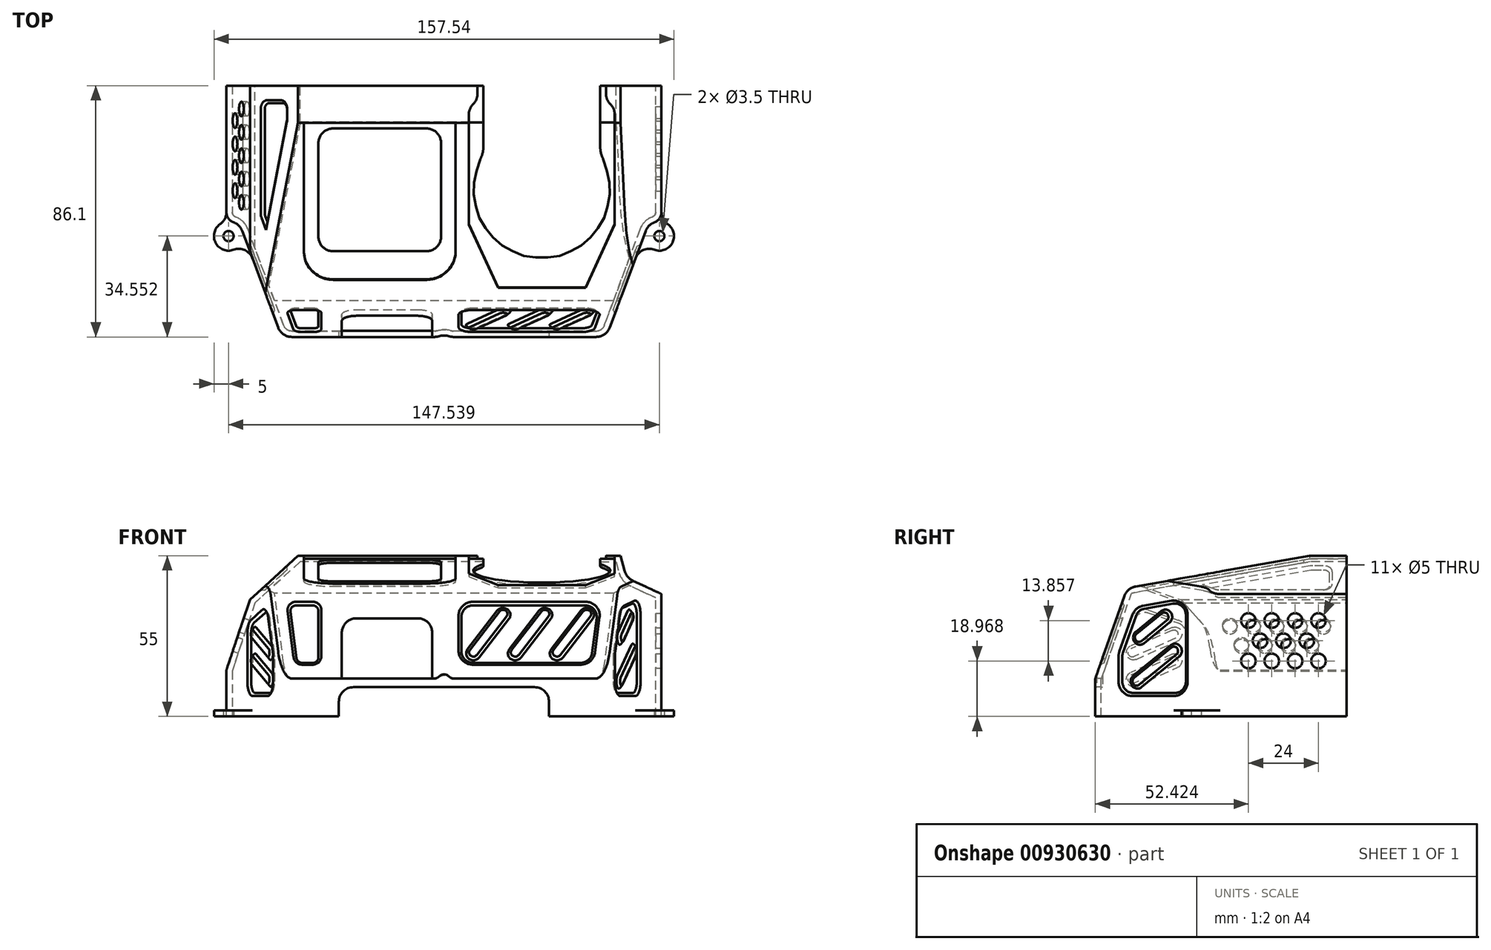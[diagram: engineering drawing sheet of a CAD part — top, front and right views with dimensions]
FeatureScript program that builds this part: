
annotation { "Feature Type Name" : "Feature", "Feature Type Description" : "" }
export const myFeature = defineFeature(function(context is Context, id is Id, definition is map)
    precondition{}
    {
        {
            var Q0;
            Q0=qCreatedBy(makeId("Top.planeOp"),FACE);
            var sketch = newSketch(context, id + "F0", { "sketchPlane" : qUnion([Q0])});
            skLineSegment(sketch, "E0.bottom", {"start": v(-53.5, -83.4) * mm, "end": v(-5, -83.4) * mm, "construction": true});
            skLineSegment(sketch, "E0.top", {"start": v(-51.5, 90.4) * mm, "end": v(51.5, 90.4) * mm, "construction": true});
            skLineSegment(sketch, "E0.left", {"start": v(-71.5, -35) * mm, "end": v(-71.5, 0) * mm, "construction": true});
            skLineSegment(sketch, "E0.right", {"start": v(71.5, -35) * mm, "end": v(71.5, 0) * mm, "construction": true});
            skLineSegment(sketch, "E1", {"start": v(-71.5, -35) * mm, "end": v(-68.01, -44.37) * mm, "construction": true});
            skLineSegment(sketch, "E2", {"start": v(53.5, -83.4) * mm, "end": v(64.53, -53.75) * mm, "construction": true});
            skPoint(sketch, "E3.orphan", {"position": v(-71.5, -83.4) * mm});
            skPoint(sketch, "E4.orphan", {"position": v(71.5, -83.4) * mm});
            skLineSegment(sketch, "E5", {"start": v(-71.5, 0) * mm, "end": v(-69.34, 9.76) * mm, "construction": true});
            skLineSegment(sketch, "E6", {"start": v(51.5, 90.4) * mm, "end": v(55.82, 70.87) * mm, "construction": true});
            skPoint(sketch, "E7.orphan", {"position": v(-71.5, 90.4) * mm});
            skPoint(sketch, "E8.orphan", {"position": v(71.5, 90.4) * mm});
            skLineSegment(sketch, "E9", {"start": v(-5, -83.4) * mm, "end": v(-5, -91.4) * mm, "construction": true});
            skLineSegment(sketch, "E10", {"start": v(5, -91.4) * mm, "end": v(5, -83.4) * mm, "construction": true});
            skArc(sketch, "E11", {"start": v(-5, -91.4) * mm, "mid": v(0, -96.4) * mm, "end": v(5, -91.4) * mm, "construction": true});
            skLineSegment(sketch, "E12.trimOffspring", {"start": v(5, -83.4) * mm, "end": v(53.5, -83.4) * mm, "construction": true});
            skLineSegment(sketch, "E13", {"start": v(-68.01, -44.37) * mm, "end": v(-75.51, -47.16) * mm, "construction": true});
            skLineSegment(sketch, "E14", {"start": v(-72.03, -56.53) * mm, "end": v(-64.53, -53.75) * mm, "construction": true});
            skArc(sketch, "E15", {"start": v(-75.51, -47.16) * mm, "mid": v(-78.46, -53.6) * mm, "end": v(-72.03, -56.53) * mm, "construction": true});
            skLineSegment(sketch, "E16.trimOffspring", {"start": v(-64.53, -53.75) * mm, "end": v(-53.5, -83.4) * mm, "construction": true});
            skLineSegment(sketch, "E17", {"start": v(68.01, -44.37) * mm, "end": v(75.51, -47.16) * mm, "construction": true});
            skLineSegment(sketch, "E18", {"start": v(72.03, -56.53) * mm, "end": v(64.53, -53.75) * mm, "construction": true});
            skArc(sketch, "E19", {"start": v(72.03, -56.53) * mm, "mid": v(78.46, -53.6) * mm, "end": v(75.51, -47.16) * mm, "construction": true});
            skLineSegment(sketch, "E20.trimOffspring", {"start": v(68.01, -44.37) * mm, "end": v(71.5, -35) * mm, "construction": true});
            skLineSegment(sketch, "E21", {"start": v(-69.34, 9.76) * mm, "end": v(-77.15, 11.5) * mm, "construction": true});
            skLineSegment(sketch, "E22.trimOffspring", {"start": v(-65.02, 29.3) * mm, "end": v(-57.98, 61.1) * mm, "construction": true});
            skLineSegment(sketch, "E23", {"start": v(69.34, 9.76) * mm, "end": v(77.15, 11.5) * mm, "construction": true});
            skLineSegment(sketch, "E24.trimOffspring", {"start": v(69.34, 9.76) * mm, "end": v(71.5, 0) * mm, "construction": true});
            skLineSegment(sketch, "E25", {"start": v(-57.98, 61.1) * mm, "end": v(-65.8, 62.84) * mm, "construction": true});
            skLineSegment(sketch, "E26", {"start": v(-55.82, 70.87) * mm, "end": v(-63.63, 72.6) * mm, "construction": true});
            skArc(sketch, "E27", {"start": v(-63.63, 72.6) * mm, "mid": v(-69.6, 68.8) * mm, "end": v(-65.8, 62.84) * mm, "construction": true});
            skLineSegment(sketch, "E28.trimOffspring", {"start": v(-55.82, 70.87) * mm, "end": v(-51.5, 90.4) * mm, "construction": true});
            skLineSegment(sketch, "E29", {"start": v(57.98, 61.1) * mm, "end": v(65.8, 62.84) * mm, "construction": true});
            skLineSegment(sketch, "E30", {"start": v(55.82, 70.87) * mm, "end": v(63.63, 72.6) * mm, "construction": true});
            skArc(sketch, "E31", {"start": v(65.8, 62.84) * mm, "mid": v(69.6, 68.8) * mm, "end": v(63.63, 72.6) * mm, "construction": true});
            skLineSegment(sketch, "E32.trimOffspring", {"start": v(57.98, 61.1) * mm, "end": v(65.02, 29.3) * mm, "construction": true});
            skCircle(sketch, "E33", {"center": v(-73.77, -51.85) * mm, "radius": 1.75 * mm, "construction": true});
            skCircle(sketch, "E34", {"center": v(-76.07, 16.37) * mm, "radius": 1.75 * mm, "construction": true});
            skCircle(sketch, "E35", {"center": v(-64.71, 67.72) * mm, "radius": 1.75 * mm, "construction": true});
            skCircle(sketch, "E36", {"center": v(64.71, 67.72) * mm, "radius": 1.75 * mm, "construction": true});
            skCircle(sketch, "E37", {"center": v(76.07, 16.37) * mm, "radius": 1.75 * mm, "construction": true});
            skCircle(sketch, "E38", {"center": v(73.77, -51.85) * mm, "radius": 1.75 * mm, "construction": true});
            skCircle(sketch, "E39", {"center": v(0, -91.4) * mm, "radius": 1.75 * mm, "construction": true});
            skCircle(sketch, "E40", {"center": v(66.5, -30) * mm, "radius": 1.75 * mm, "construction": true});
            skCircle(sketch, "E41", {"center": v(28.5, 0.5) * mm, "radius": 1.75 * mm, "construction": true});
            skCircle(sketch, "E42", {"center": v(-57, -10) * mm, "radius": 1.75 * mm, "construction": true});
            skCircle(sketch, "E43", {"center": v(-57, -56) * mm, "radius": 1.75 * mm, "construction": true});
            skCircle(sketch, "E44", {"center": v(28.5, -66.5) * mm, "radius": 1.75 * mm, "construction": true});
            skArc(sketch, "E45", {"start": v(-59.92, -5.94) * mm, "mid": v(-61.45, -7.72) * mm, "end": v(-62, -10) * mm, "construction": true});
            skLineSegment(sketch, "E46", {"start": v(-62, -10) * mm, "end": v(-62, -56) * mm, "construction": true});
            skArc(sketch, "E47", {"start": v(-62, -56) * mm, "mid": v(-61.43, -58.31) * mm, "end": v(-59.86, -60.1) * mm, "construction": true});
            skArc(sketch, "E48", {"start": v(28.5, -71.5) * mm, "mid": v(32.04, -70.04) * mm, "end": v(33.5, -66.5) * mm, "construction": true});
            skArc(sketch, "E49", {"start": v(33.5, 0.5) * mm, "mid": v(32.04, 4.04) * mm, "end": v(28.5, 5.5) * mm, "construction": true});
            skArc(sketch, "E50", {"start": v(71.5, -9.75) * mm, "mid": v(69.95, -6.38) * mm, "end": v(66.5, -5) * mm, "construction": true});
            skArc(sketch, "E51", {"start": v(58.36, -61) * mm, "mid": v(61.2, -60.1) * mm, "end": v(63.04, -57.74) * mm, "construction": true});
            skLineSegment(sketch, "E52", {"start": v(28.5, -71.5) * mm, "end": v(-43.5, -71.5) * mm, "construction": true});
            skLineSegment(sketch, "E53", {"start": v(-43.5, -71.5) * mm, "end": v(-59.86, -60.1) * mm, "construction": true});
            skLineSegment(sketch, "E54", {"start": v(-59.92, -5.94) * mm, "end": v(-44, 5.5) * mm, "construction": true});
            skLineSegment(sketch, "E55", {"start": v(-44, 5.5) * mm, "end": v(28.5, 5.5) * mm, "construction": true});
            skLineSegment(sketch, "E56", {"start": v(33.5, 0.5) * mm, "end": v(33.5, -5) * mm, "construction": true});
            skLineSegment(sketch, "E57", {"start": v(33.5, -5) * mm, "end": v(66.5, -5) * mm, "construction": true});
            skLineSegment(sketch, "E58", {"start": v(33.5, -66.5) * mm, "end": v(33.5, -61) * mm, "construction": true});
            skLineSegment(sketch, "E59", {"start": v(33.5, -61) * mm, "end": v(58.36, -61) * mm, "construction": true});
            skCircle(sketch, "E60", {"center": v(-22, -36) * mm, "radius": 18.8 * mm, "construction": true});
            skCircle(sketch, "E61", {"center": v(20.5, -18) * mm, "radius": 1.5 * mm, "construction": true});
            skCircle(sketch, "E62", {"center": v(46.5, -18) * mm, "radius": 1.5 * mm, "construction": true});
            skCircle(sketch, "E63", {"center": v(20.5, -48) * mm, "radius": 1.5 * mm, "construction": true});
            skCircle(sketch, "E64", {"center": v(46.5, -48) * mm, "radius": 1.5 * mm, "construction": true});
            skLineSegment(sketch, "E65", {"start": v(17, -6) * mm, "end": v(17, -48) * mm, "construction": true});
            skLineSegment(sketch, "E66", {"start": v(50, -6) * mm, "end": v(50, -48) * mm, "construction": true});
            skLineSegment(sketch, "E67", {"start": v(20.5, -51.5) * mm, "end": v(46.5, -51.5) * mm, "construction": true});
            skArc(sketch, "E68", {"start": v(17, -48) * mm, "mid": v(18.03, -50.47) * mm, "end": v(20.5, -51.5) * mm, "construction": true});
            skArc(sketch, "E69", {"start": v(46.5, -51.5) * mm, "mid": v(48.97, -50.47) * mm, "end": v(50, -48) * mm, "construction": true});
            skLineSegment(sketch, "E70", {"start": v(17, -6) * mm, "end": v(50, -6) * mm, "construction": true});
            skLineSegment(sketch, "E71", {"start": v(-80.95, 17.45) * mm, "end": v(-78.8, 27.22) * mm, "construction": true});
            skArc(sketch, "E72", {"start": v(-80.95, 17.45) * mm, "mid": v(-80.29, 13.69) * mm, "end": v(-77.15, 11.5) * mm, "construction": true});
            skArc(sketch, "E73", {"start": v(-72.83, 31.02) * mm, "mid": v(-76.6, 30.35) * mm, "end": v(-78.8, 27.22) * mm, "construction": true});
            skLineSegment(sketch, "E74", {"start": v(-72.83, 31.02) * mm, "end": v(-65.02, 29.3) * mm, "construction": true});
            skCircle(sketch, "E75", {"center": v(-73.91, 26.14) * mm, "radius": 1.75 * mm, "construction": true});
            skLineSegment(sketch, "E76", {"start": v(65.02, 29.3) * mm, "end": v(72.83, 31.02) * mm, "construction": true});
            skArc(sketch, "E77", {"start": v(78.8, 27.22) * mm, "mid": v(76.6, 30.35) * mm, "end": v(72.83, 31.02) * mm, "construction": true});
            skArc(sketch, "E78", {"start": v(77.15, 11.5) * mm, "mid": v(80.29, 13.69) * mm, "end": v(80.95, 17.45) * mm, "construction": true});
            skLineSegment(sketch, "E79", {"start": v(78.8, 27.22) * mm, "end": v(80.95, 17.45) * mm, "construction": true});
            skCircle(sketch, "E80", {"center": v(73.91, 26.14) * mm, "radius": 1.75 * mm, "construction": true});
            skLineSegment(sketch, "E81", {"start": v(-43, -19.9) * mm, "end": v(-43, -52.1) * mm, "construction": true});
            skLineSegment(sketch, "E82", {"start": v(-38.1, -57) * mm, "end": v(-5.9, -57) * mm, "construction": true});
            skLineSegment(sketch, "E83", {"start": v(-1, -52.1) * mm, "end": v(-1, -19.9) * mm, "construction": true});
            skLineSegment(sketch, "E84", {"start": v(-5.9, -15) * mm, "end": v(-38.1, -15) * mm, "construction": true});
            skArc(sketch, "E85", {"start": v(-38.1, -15) * mm, "mid": v(-41.56, -16.44) * mm, "end": v(-43, -19.9) * mm, "construction": true});
            skArc(sketch, "E86", {"start": v(-43, -52.1) * mm, "mid": v(-41.56, -55.56) * mm, "end": v(-38.1, -57) * mm, "construction": true});
            skArc(sketch, "E87", {"start": v(-1, -19.9) * mm, "mid": v(-2.44, -16.44) * mm, "end": v(-5.9, -15) * mm, "construction": true});
            skArc(sketch, "E88", {"start": v(-5.9, -57) * mm, "mid": v(-2.44, -55.56) * mm, "end": v(-1, -52.1) * mm, "construction": true});
            skCircle(sketch, "E89", {"center": v(33.5, -36) * mm, "radius": 23.5 * mm, "construction": true});
            skSolve(sketch);
        }
        {
            var Q0;
            Q0=qCreatedBy(makeId("Top.planeOp"),FACE);
            var sketch = newSketch(context, id + "F1", { "sketchPlane" : qUnion([Q0])});
            skLineSegment(sketch, "E90", {"start": v(-74.5, 0) * mm, "end": v(74.5, 0) * mm});
            skLineSegment(sketch, "E91", {"start": v(-74.5, 0) * mm, "end": v(-74.5, -46.78) * mm});
            skLineSegment(sketch, "E92", {"start": v(74.5, -46.78) * mm, "end": v(74.5, 0) * mm});
            skLineSegment(sketch, "E93", {"start": v(-67.34, -54.8) * mm, "end": v(-55.59, -86.4) * mm});
            skLineSegment(sketch, "E94", {"start": v(55.59, -86.4) * mm, "end": v(67.34, -54.8) * mm});
            skLineSegment(sketch, "E95.trimOffspring", {"start": v(-55.59, -86.4) * mm, "end": v(-2.3, -86.4) * mm});
            skArc(sketch, "E96", {"start": v(-75.51, -47.16) * mm, "mid": v(-78.46, -53.6) * mm, "end": v(-72.03, -56.53) * mm});
            skLineSegment(sketch, "E97", {"start": v(-75.51, -47.16) * mm, "end": v(-74.5, -46.78) * mm});
            skLineSegment(sketch, "E98", {"start": v(-72.03, -56.53) * mm, "end": v(-67.34, -54.8) * mm});
            skLineSegment(sketch, "E99", {"start": v(67.34, -54.8) * mm, "end": v(72.03, -56.53) * mm});
            skLineSegment(sketch, "E100", {"start": v(74.5, -46.78) * mm, "end": v(75.51, -47.16) * mm});
            skArc(sketch, "E101", {"start": v(72.03, -56.53) * mm, "mid": v(78.46, -53.6) * mm, "end": v(75.51, -47.16) * mm});
            skArc(sketch, "E102", {"start": v(2.3, -86.4) * mm, "mid": v(0, -85.9) * mm, "end": v(-2.3, -86.4) * mm});
            skLineSegment(sketch, "E103.trimOffspring", {"start": v(2.3, -86.4) * mm, "end": v(55.59, -86.4) * mm});
            skSolve(sketch);
        }
        {
            var Q0;
            Q0=qSketchRegion(id+"F1",true);
            extrude(context, id + "F2", {"entities" : qUnion([Q0]), "depth" : 55 * mm, "offsetDistance" : 25 * mm});
        }
        {
            var Q0;
            Q0=makeQuery(id+"F2.opExtrude","SWEPT_EDGE",EDGE,{"disambiguationData":[OSD([sQuery(id+"F1.wireOp",EDGE,"E93"),sQuery(id+"F1.wireOp",EDGE,"3QDwpkBZ-OKoi-ct7H-oCOv-kOIZgjfHdJRy")])]});
            var Q1;
            Q1=makeQuery(id+"F2.opExtrude","SWEPT_EDGE",EDGE,{"disambiguationData":[OSD([sQuery(id+"F1.wireOp",EDGE,"E93"),sQuery(id+"F1.wireOp",EDGE,"E95.trimOffspring")])]});
            var Q2;
            Q2=makeQuery(id+"F2.opExtrude","SWEPT_EDGE",EDGE,{"disambiguationData":[OSD([sQuery(id+"F1.wireOp",EDGE,"E94"),sQuery(id+"F1.wireOp",EDGE,"E95.trimOffspring")])]});
            var Q3;
            Q3=makeQuery(id+"F2.opExtrude","SWEPT_EDGE",EDGE,{"disambiguationData":[OSD([sQuery(id+"F1.wireOp",EDGE,"E94"),sQuery(id+"F1.wireOp",EDGE,"8AUUyvxQ-JrK8-Af2P-wNva-NpeGH8QvNI9z")])]});
            var Q4;
            Q4=makeQuery(id+"F2.opExtrude","SWEPT_EDGE",EDGE,{"disambiguationData":[OSD([sQuery(id+"F1.wireOp",EDGE,"E91"),sQuery(id+"F1.wireOp",EDGE,"E97")])]});
            var Q5;
            Q5=makeQuery(id+"F2.opExtrude","SWEPT_EDGE",EDGE,{"disambiguationData":[OSD([sQuery(id+"F1.wireOp",EDGE,"E92"),sQuery(id+"F1.wireOp",EDGE,"E100")])]});
            var Q6;
            Q6=makeQuery(id+"F2.opExtrude","SWEPT_EDGE",EDGE,{"disambiguationData":[OSD([sQuery(id+"F1.wireOp",EDGE,"E102"),sQuery(id+"F1.wireOp",EDGE,"E103.trimOffspring")])]});
            fillet(context, id + "F3", {"entities" : qUnion([Q0, Q1, Q2, Q3, Q4, Q5, Q6]), "radius" : 5 * mm, "tangentPropagation" : true, "allowEdgeOverflow" : false});
        }
        {
            var Q0;
            Q0=makeQuery(id+"F2.opExtrude","SWEPT_FACE",FACE,{"disambiguationData":[OSD([sQuery(id+"F1.wireOp",EDGE,"E90")])]});
            var sketch = newSketch(context, id + "F4", { "sketchPlane" : qUnion([Q0])});
            skLineSegment(sketch, "E104.bottom", {"start": v(-71.5, 13) * mm, "end": v(71.5, 13) * mm, "construction": true});
            skLineSegment(sketch, "E104.top", {"start": v(-71.5, 10) * mm, "end": v(71.5, 10) * mm, "construction": true});
            skLineSegment(sketch, "E104.left", {"start": v(-71.5, 13) * mm, "end": v(-71.5, 10) * mm, "construction": true});
            skLineSegment(sketch, "E104.right", {"start": v(71.5, 13) * mm, "end": v(71.5, 10) * mm, "construction": true});
            skLineSegment(sketch, "E105.bottom", {"start": v(-71.5, 40) * mm, "end": v(62, 40) * mm, "construction": true});
            skLineSegment(sketch, "E105.top", {"start": v(-71.5, 38) * mm, "end": v(62, 38) * mm, "construction": true});
            skLineSegment(sketch, "E105.left", {"start": v(-71.5, 40) * mm, "end": v(-71.5, 38) * mm, "construction": true});
            skLineSegment(sketch, "E105.right", {"start": v(62, 40) * mm, "end": v(62, 38) * mm, "construction": true});
            skLineSegment(sketch, "E106", {"start": v(-71.5, 38) * mm, "end": v(-71.5, 13) * mm, "construction": true});
            skLineSegment(sketch, "E107", {"start": v(-61.5, 38) * mm, "end": v(-61.5, 13) * mm, "construction": true});
            skLineSegment(sketch, "E108", {"start": v(62, 38) * mm, "end": v(62, 13) * mm, "construction": true});
            skLineSegment(sketch, "E109", {"start": v(52, 38) * mm, "end": v(52, 13) * mm, "construction": true});
            skLineSegment(sketch, "E110", {"start": v(-50, 40) * mm, "end": v(-50, 50) * mm, "construction": true});
            skLineSegment(sketch, "E111", {"start": v(-50, 50) * mm, "end": v(-17, 50) * mm, "construction": true});
            skLineSegment(sketch, "E112", {"start": v(-17, 50) * mm, "end": v(-17, 40) * mm, "construction": true});
            skLineSegment(sketch, "E113", {"start": v(43, 40) * mm, "end": v(43, 48) * mm, "construction": true});
            skLineSegment(sketch, "E114", {"start": v(43, 48) * mm, "end": v(1, 48) * mm, "construction": true});
            skLineSegment(sketch, "E115", {"start": v(1, 48) * mm, "end": v(1, 40) * mm, "construction": true});
            skSolve(sketch);
        }
        {
            var Q0;
            Q0=qCreatedBy(makeId("Right.planeOp"),FACE);
            var sketch = newSketch(context, id + "F5", { "sketchPlane" : qUnion([Q0])});
            skLineSegment(sketch, "E116.bottom", {"start": v(5.5, 13) * mm, "end": v(-77.9, 13) * mm, "construction": true});
            skLineSegment(sketch, "E116.top", {"start": v(5.5, 10) * mm, "end": v(-77.9, 10) * mm, "construction": true});
            skLineSegment(sketch, "E116.left", {"start": v(5.5, 13) * mm, "end": v(5.5, 10) * mm, "construction": true});
            skLineSegment(sketch, "E116.right", {"start": v(-77.9, 13) * mm, "end": v(-77.9, 10) * mm, "construction": true});
            skLineSegment(sketch, "E117.bottom", {"start": v(5.5, 40) * mm, "end": v(-71.5, 40) * mm, "construction": true});
            skLineSegment(sketch, "E117.top", {"start": v(5.5, 38) * mm, "end": v(-71.5, 38) * mm, "construction": true});
            skLineSegment(sketch, "E117.left", {"start": v(5.5, 40) * mm, "end": v(5.5, 38) * mm, "construction": true});
            skLineSegment(sketch, "E117.right", {"start": v(-71.5, 40) * mm, "end": v(-71.5, 38) * mm, "construction": true});
            skLineSegment(sketch, "E118", {"start": v(-71.5, 38) * mm, "end": v(-71.5, 13) * mm, "construction": true});
            skLineSegment(sketch, "E119", {"start": v(-61.5, 38) * mm, "end": v(-61.5, 13) * mm, "construction": true});
            skLineSegment(sketch, "E120", {"start": v(5.5, 38) * mm, "end": v(5.5, 13) * mm, "construction": true});
            skLineSegment(sketch, "E121", {"start": v(-4.5, 38) * mm, "end": v(-4.5, 13) * mm, "construction": true});
            skLineSegment(sketch, "E122", {"start": v(-15, 40) * mm, "end": v(-15, 48) * mm, "construction": true});
            skLineSegment(sketch, "E123", {"start": v(-15, 48) * mm, "end": v(-57, 48) * mm, "construction": true});
            skLineSegment(sketch, "E124", {"start": v(-57, 48) * mm, "end": v(-57, 40) * mm, "construction": true});
            skSolve(sketch);
        }
        {
            var Q0;
            Q0=makeQuery(id+"F2.opExtrude","SWEPT_FACE",FACE,{"disambiguationData":[OSD([sQuery(id+"F1.wireOp",EDGE,"E91")])]});
            var sketch = newSketch(context, id + "F6", { "sketchPlane" : qUnion([Q0])});
            skLineSegment(sketch, "E125", {"start": v(13, 55) * mm, "end": v(75.5, 44) * mm});
            skLineSegment(sketch, "E126", {"start": v(75.5, 44) * mm, "end": v(86.4, 13) * mm});
            skLineSegment(sketch, "E127", {"start": v(13, 55) * mm, "end": v(86.4, 55) * mm});
            skLineSegment(sketch, "E128", {"start": v(86.4, 55) * mm, "end": v(86.4, 13) * mm});
            skSolve(sketch);
        }
        {
            var Q0;
            Q0=qSketchRegion(id+"F6",true);
            extrude(context, id + "F7", {"entities" : qUnion([Q0]), "operationType" : NewBodyOperationType.REMOVE, "endBound" : BoundingType.THROUGH_ALL, "oppositeDirection" : true, "depth" : 25 * mm, "offsetDistance" : 25 * mm});
        }
        {
            var Q0;
            Q0=qSketchRegion(id+"F6",true);
            extrude(context, id + "F8", {"entities" : qUnion([Q0]), "operationType" : NewBodyOperationType.REMOVE, "endBound" : BoundingType.THROUGH_ALL, "depth" : 25 * mm, "offsetDistance" : 25 * mm});
        }
        {
            var Q0;
            {var subQ0=sQuery(id+"F1.wireOp",EDGE,"E90");Q0=makeQuery(id+"F4.imprint","IMPRINT",FACE,{"disambiguationData":[TD([[makeQuery(id+"F4.imprint","IMPRINT",EDGE,{"derivedFrom":makeQuery(id+"F2.opExtrude","CAP_EDGE",EDGE,{"disambiguationData":[OSD([subQ0])],"isStart":true})}),-1.0]])]});}
            var sketch = newSketch(context, id + "F9", { "sketchPlane" : qUnion([Q0])});
            skLineSegment(sketch, "E129", {"start": v(50, 55) * mm, "end": v(66.45, 40) * mm});
            skLineSegment(sketch, "E130", {"start": v(66.45, 40) * mm, "end": v(78.8, 3) * mm});
            skLineSegment(sketch, "E131", {"start": v(50, 55) * mm, "end": v(78.8, 55) * mm});
            skLineSegment(sketch, "E132", {"start": v(-78.8, 39.91) * mm, "end": v(-62.51, 47.49) * mm});
            skLineSegment(sketch, "E133", {"start": v(-60.5, 55) * mm, "end": v(-78.8, 55) * mm});
            skLineSegment(sketch, "E134", {"start": v(78.8, 55) * mm, "end": v(78.8, 3) * mm});
            skLineSegment(sketch, "E135", {"start": v(-78.8, 55) * mm, "end": v(-78.8, 39.91) * mm});
            skLineSegment(sketch, "E136", {"start": v(-60.5, 55) * mm, "end": v(-62.51, 47.49) * mm});
            skSolve(sketch);
        }
        {
            var Q0;
            Q0=qSketchRegion(id+"F9",true);
            var Q1;
            Q1=makeQuery(id+"F2.opExtrude","SWEPT_FACE",FACE,{"disambiguationData":[OSD([sQuery(id+"F1.wireOp",EDGE,"E95.trimOffspring")])]});
            extrude(context, id + "F10", {"entities" : qUnion([Q0]), "operationType" : NewBodyOperationType.REMOVE, "endBound" : BoundingType.UP_TO_SURFACE, "oppositeDirection" : true, "depth" : 25 * mm, "endBoundEntityFace" : qUnion([Q1]), "offsetDistance" : 25 * mm});
        }
        {
            var Q0;
            Q0=makeQuery(id+"F2.opExtrude","CAP_FACE",FACE,{"disambiguationData":[OSD([sQuery(id+"F1.wireOp",EDGE,"E90"),sQuery(id+"F1.wireOp",EDGE,"E91"),sQuery(id+"F1.wireOp",EDGE,"E92"),sQuery(id+"F1.wireOp",EDGE,"E93"),sQuery(id+"F1.wireOp",EDGE,"E94"),sQuery(id+"F1.wireOp",EDGE,"E95.trimOffspring"),sQuery(id+"F1.wireOp",EDGE,"3QDwpkBZ-OKoi-ct7H-oCOv-kOIZgjfHdJRy"),sQuery(id+"F1.wireOp",EDGE,"8AUUyvxQ-JrK8-Af2P-wNva-NpeGH8QvNI9z")])],"isStart":false});
            var sketch = newSketch(context, id + "F11", { "sketchPlane" : qUnion([Q0])});
            skArc(sketch, "E137", {"start": v(-76.63, -47.75) * mm, "mid": v(-78.2, -54.17) * mm, "end": v(-72.03, -56.53) * mm});
            skArc(sketch, "E138", {"start": v(-76.63, -47.75) * mm, "mid": v(-75.07, -45.96) * mm, "end": v(-74.5, -43.65) * mm});
            skArc(sketch, "E139", {"start": v(72.05, -47.15) * mm, "mid": v(70.24, -48.3) * mm, "end": v(69.08, -50.1) * mm});
            skArc(sketch, "E140", {"start": v(72.05, -47.15) * mm, "mid": v(73.83, -45.79) * mm, "end": v(74.5, -43.65) * mm});
            skLineSegment(sketch, "E141", {"start": v(65.6, -59.48) * mm, "end": v(69.08, -50.1) * mm});
            skArc(sketch, "E142", {"start": v(74.5, -43.65) * mm, "mid": v(75.07, -45.96) * mm, "end": v(76.63, -47.75) * mm});
            skArc(sketch, "E143", {"start": v(72.03, -56.53) * mm, "mid": v(68.2, -56.67) * mm, "end": v(65.6, -59.48) * mm});
            skArc(sketch, "E144.trimOffspring", {"start": v(72.03, -56.53) * mm, "mid": v(78.2, -54.17) * mm, "end": v(76.63, -47.75) * mm});
            skLineSegment(sketch, "E145", {"start": v(-69.08, -50.1) * mm, "end": v(-65.6, -59.48) * mm});
            skArc(sketch, "E146", {"start": v(-65.6, -59.48) * mm, "mid": v(-68.2, -56.67) * mm, "end": v(-72.03, -56.53) * mm});
            skArc(sketch, "E147", {"start": v(-74.5, -43.65) * mm, "mid": v(-73.83, -45.79) * mm, "end": v(-72.05, -47.15) * mm});
            skArc(sketch, "E148", {"start": v(-69.08, -50.1) * mm, "mid": v(-70.24, -48.3) * mm, "end": v(-72.05, -47.15) * mm});
            skSolve(sketch);
        }
        {
            var Q0;
            Q0=qSketchRegion(id+"F11",true);
            extrude(context, id + "F12", {"entities" : qUnion([Q0]), "operationType" : NewBodyOperationType.REMOVE, "oppositeDirection" : true, "depth" : 53 * mm, "offsetDistance" : 25 * mm});
        }
        {
            var Q0;
            Q0=makeQuery(id+"F10.boolean.opBoolean","COPY",EDGE,{"derivedFrom":makeQuery(id+"F10.opExtrude","SWEPT_EDGE",EDGE,{"disambiguationData":[OSD([sQuery(id+"F9.wireOp",EDGE,"E132"),sQuery(id+"F9.wireOp",EDGE,"E136")])]})});
            fillet(context, id + "F13", {"entities" : qUnion([Q0]), "radius" : 5 * mm, "tangentPropagation" : true, "allowEdgeOverflow" : false});
        }
        {
            var Q0;
            Q0=makeQuery(id+"F2.opExtrude","CAP_FACE",FACE,{"disambiguationData":[OSD([sQuery(id+"F1.wireOp",EDGE,"E90"),sQuery(id+"F1.wireOp",EDGE,"E91"),sQuery(id+"F1.wireOp",EDGE,"E92"),sQuery(id+"F1.wireOp",EDGE,"E93"),sQuery(id+"F1.wireOp",EDGE,"GGPhoMr7-LLCb-cDVK-JcuQ-zph5waWRomu5"),sQuery(id+"F1.wireOp",EDGE,"E94"),sQuery(id+"F1.wireOp",EDGE,"9VBcLSkf-SVc8-PxgQ-01uj-v3Ae6aV1uuf6"),sQuery(id+"F1.wireOp",EDGE,"z1RWJUp2-9iWF-WXYc-lacg-Vl37dujnkeev"),sQuery(id+"F1.wireOp",EDGE,"V8AFj6se-cQ2d-STFe-ODbp-G1NrC8Z3xqAU"),sQuery(id+"F1.wireOp",EDGE,"E95.trimOffspring")])],"isStart":true});
            var Q1;
            Q1=makeQuery(id+"F2.opExtrude","SWEPT_FACE",FACE,{"disambiguationData":[OSD([sQuery(id+"F1.wireOp",EDGE,"E90")])]});
            shell(context, id + "F14", {"entities" : qUnion([Q0, Q1]), "thickness" : 2 * mm});
        }
        {
            var Q0;
            Q0=makeQuery(id+"F7.boolean.opBoolean","COPY",EDGE,{"derivedFrom":makeQuery(id+"F7.opExtrude","SWEPT_EDGE",EDGE,{"disambiguationData":[OSD([sQuery(id+"F6.wireOp",EDGE,"E125"),sQuery(id+"F6.wireOp",EDGE,"E126")])]})});
            fillet(context, id + "F15", {"entities" : qUnion([Q0]), "radius" : 5 * mm, "tangentPropagation" : true, "allowEdgeOverflow" : false});
        }
        {
            var Q0;
            {var subQ0=sQuery(id+"F1.wireOp",EDGE,"E90");var subQ1=sQuery(id+"F1.wireOp",EDGE,"E91");var subQ2=sQuery(id+"F1.wireOp",EDGE,"E92");Q0=makeQuery(id+"F7.boolean.opBoolean","SPLIT",FACE,{"disambiguationData":[TD([makeQuery(id+"F2.opExtrude","SWEPT_FACE",FACE,{"disambiguationData":[OSD([subQ0])]})])],"derivedFrom":makeQuery(id+"F2.opExtrude","CAP_FACE",FACE,{"disambiguationData":[OSD([subQ0,subQ1,subQ2,sQuery(id+"F1.wireOp",EDGE,"E93"),sQuery(id+"F1.wireOp",EDGE,"E94"),sQuery(id+"F1.wireOp",EDGE,"E95.trimOffspring"),sQuery(id+"F1.wireOp",EDGE,"E96"),sQuery(id+"F1.wireOp",EDGE,"E97"),sQuery(id+"F1.wireOp",EDGE,"E98"),sQuery(id+"F1.wireOp",EDGE,"E99"),sQuery(id+"F1.wireOp",EDGE,"E100"),sQuery(id+"F1.wireOp",EDGE,"E101"),sQuery(id+"F1.wireOp",EDGE,"E102"),sQuery(id+"F1.wireOp",EDGE,"E103.trimOffspring")])],"isStart":false})});}
            var sketch = newSketch(context, id + "F16", { "sketchPlane" : qUnion([Q0])});
            skLineSegment(sketch, "E149.bottom", {"start": v(-43, -15) * mm, "end": v(-1, -15) * mm});
            skLineSegment(sketch, "E149.top", {"start": v(-43, -57) * mm, "end": v(-1, -57) * mm});
            skLineSegment(sketch, "E149.left", {"start": v(-43, -15) * mm, "end": v(-43, -57) * mm});
            skLineSegment(sketch, "E149.right", {"start": v(-1, -15) * mm, "end": v(-1, -57) * mm});
            skSolve(sketch);
        }
        {
            var Q0;
            Q0=qSketchRegion(id+"F16",true);
            var Q1;
            Q1=makeQuery(id+"F14.opShell","OFFSET_FACE",FACE,{"disambiguationData":[OSD([sQuery(id+"F6.wireOp",EDGE,"E125")])]});
            extrude(context, id + "F17", {"entities" : qUnion([Q0]), "operationType" : NewBodyOperationType.REMOVE, "endBound" : BoundingType.UP_TO_SURFACE, "oppositeDirection" : true, "depth" : 25 * mm, "endBoundEntityFace" : qUnion([Q1]), "offsetDistance" : 25 * mm});
        }
        {
            var Q0;
            {var subQ0=sQuery(id+"F1.wireOp",EDGE,"E90");var subQ1=sQuery(id+"F1.wireOp",EDGE,"E91");var subQ2=sQuery(id+"F1.wireOp",EDGE,"E92");Q0=makeQuery(id+"F7.boolean.opBoolean","SPLIT",FACE,{"disambiguationData":[TD([makeQuery(id+"F2.opExtrude","SWEPT_FACE",FACE,{"disambiguationData":[OSD([subQ0])]})])],"derivedFrom":makeQuery(id+"F2.opExtrude","CAP_FACE",FACE,{"disambiguationData":[OSD([subQ0,subQ1,subQ2,sQuery(id+"F1.wireOp",EDGE,"E93"),sQuery(id+"F1.wireOp",EDGE,"E94"),sQuery(id+"F1.wireOp",EDGE,"E95.trimOffspring"),sQuery(id+"F1.wireOp",EDGE,"E96"),sQuery(id+"F1.wireOp",EDGE,"E97"),sQuery(id+"F1.wireOp",EDGE,"E98"),sQuery(id+"F1.wireOp",EDGE,"E99"),sQuery(id+"F1.wireOp",EDGE,"E100"),sQuery(id+"F1.wireOp",EDGE,"E101"),sQuery(id+"F1.wireOp",EDGE,"E102"),sQuery(id+"F1.wireOp",EDGE,"E103.trimOffspring")])],"isStart":false})});}
            var sketch = newSketch(context, id + "F18", { "sketchPlane" : qUnion([Q0])});
            skLineSegment(sketch, "E150.bottom", {"start": v(13.5, 0) * mm, "end": v(53.5, 0.06) * mm});
            skLineSegment(sketch, "E150.left", {"start": v(13.5, 0) * mm, "end": v(13.5, -21.1) * mm});
            skLineSegment(sketch, "E150.right", {"start": v(53.5, 0.06) * mm, "end": v(53.5, -21.1) * mm});
            skLineSegment(sketch, "E151", {"start": v(33.5, 0.03) * mm, "end": v(33.5, -59.5) * mm, "construction": true});
            skArc(sketch, "E152", {"start": v(12.46, -25.54) * mm, "mid": v(33.5, -59.5) * mm, "end": v(54.54, -25.54) * mm});
            skPoint(sketch, "E153.visualSharp", {"position": v(13.5, -23.66) * mm});
            skArc(sketch, "E153.filletArc", {"start": v(12.46, -25.54) * mm, "mid": v(13.24, -23.38) * mm, "end": v(13.5, -21.1) * mm});
            skPoint(sketch, "E154.visualSharp", {"position": v(53.5, -23.66) * mm});
            skArc(sketch, "E154.filletArc", {"start": v(53.5, -21.1) * mm, "mid": v(53.76, -23.38) * mm, "end": v(54.54, -25.54) * mm});
            skSolve(sketch);
        }
        {
            var Q0;
            Q0=qSketchRegion(id+"F18",true);
            extrude(context, id + "F19", {"entities" : qUnion([Q0]), "operationType" : NewBodyOperationType.REMOVE, "endBound" : BoundingType.THROUGH_ALL, "oppositeDirection" : true, "depth" : 25 * mm, "offsetDistance" : 25 * mm});
        }
        {
            var Q0;
            Q0=makeQuery(id+"F17.boolean.opBoolean","COPY",EDGE,{"derivedFrom":makeQuery(id+"F17.opExtrude","SWEPT_EDGE",EDGE,{"disambiguationData":[OSD([sQuery(id+"F16.wireOp",EDGE,"E149.bottom"),sQuery(id+"F16.wireOp",EDGE,"E149.left")])]})});
            var Q1;
            Q1=makeQuery(id+"F17.boolean.opBoolean","COPY",EDGE,{"derivedFrom":makeQuery(id+"F17.opExtrude","SWEPT_EDGE",EDGE,{"disambiguationData":[OSD([sQuery(id+"F16.wireOp",EDGE,"E149.bottom"),sQuery(id+"F16.wireOp",EDGE,"E149.right")])]})});
            var Q2;
            Q2=makeQuery(id+"F17.boolean.opBoolean","COPY",EDGE,{"derivedFrom":makeQuery(id+"F17.opExtrude","SWEPT_EDGE",EDGE,{"disambiguationData":[OSD([sQuery(id+"F16.wireOp",EDGE,"E149.top"),sQuery(id+"F16.wireOp",EDGE,"E149.left")])]})});
            var Q3;
            Q3=makeQuery(id+"F17.boolean.opBoolean","COPY",EDGE,{"derivedFrom":makeQuery(id+"F17.opExtrude","SWEPT_EDGE",EDGE,{"disambiguationData":[OSD([sQuery(id+"F16.wireOp",EDGE,"E149.top"),sQuery(id+"F16.wireOp",EDGE,"E149.right")])]})});
            fillet(context, id + "F20", {"entities" : qUnion([Q0, Q1, Q2, Q3]), "radius" : 4.9 * mm, "tangentPropagation" : true, "allowEdgeOverflow" : false});
        }
        {
            var Q0;
            Q0=makeQuery(id+"F2.opExtrude","SWEPT_FACE",FACE,{"disambiguationData":[OSD([sQuery(id+"F1.wireOp",EDGE,"E95.trimOffspring")])]});
            var sketch = newSketch(context, id + "F21", { "sketchPlane" : qUnion([Q0])});
            skLineSegment(sketch, "E155.bottom", {"start": v(-35, 13) * mm, "end": v(-4, 13) * mm});
            skLineSegment(sketch, "E155.top", {"start": v(-35, 33.6) * mm, "end": v(-4, 33.6) * mm});
            skLineSegment(sketch, "E155.left", {"start": v(-35, 13) * mm, "end": v(-35, 33.6) * mm});
            skLineSegment(sketch, "E155.right", {"start": v(-4, 13) * mm, "end": v(-4, 33.6) * mm});
            skSolve(sketch);
        }
        {
            var Q0;
            Q0=qSketchRegion(id+"F21",true);
            var Q1;
            Q1=makeQuery(id+"F14.opShell","OFFSET_FACE",FACE,{"disambiguationData":[OSD([sQuery(id+"F6.wireOp",EDGE,"E126")])]});
            extrude(context, id + "F22", {"entities" : qUnion([Q0]), "operationType" : NewBodyOperationType.REMOVE, "endBound" : BoundingType.UP_TO_SURFACE, "oppositeDirection" : true, "depth" : 25 * mm, "endBoundEntityFace" : qUnion([Q1]), "offsetDistance" : 25 * mm});
        }
        {
            var Q0;
            Q0=makeQuery(id+"F22.boolean.opBoolean","COPY",EDGE,{"derivedFrom":makeQuery(id+"F22.opExtrude","SWEPT_EDGE",EDGE,{"disambiguationData":[OSD([sQuery(id+"F21.wireOp",EDGE,"E155.top"),sQuery(id+"F21.wireOp",EDGE,"E155.left")])]})});
            var Q1;
            Q1=makeQuery(id+"F22.boolean.opBoolean","COPY",EDGE,{"derivedFrom":makeQuery(id+"F22.opExtrude","SWEPT_EDGE",EDGE,{"disambiguationData":[OSD([sQuery(id+"F21.wireOp",EDGE,"E155.top"),sQuery(id+"F21.wireOp",EDGE,"E155.right")])]})});
            fillet(context, id + "F23", {"entities" : qUnion([Q0, Q1]), "radius" : 5 * mm, "tangentPropagation" : true, "allowEdgeOverflow" : false});
        }
        {
            var Q0;
            Q0=makeQuery(id+"F2.opExtrude","CAP_FACE",FACE,{"disambiguationData":[OSD([sQuery(id+"F1.wireOp",EDGE,"E90"),sQuery(id+"F1.wireOp",EDGE,"E91"),sQuery(id+"F1.wireOp",EDGE,"E92"),sQuery(id+"F1.wireOp",EDGE,"E93"),sQuery(id+"F1.wireOp",EDGE,"E94"),sQuery(id+"F1.wireOp",EDGE,"E95.trimOffspring"),sQuery(id+"F1.wireOp",EDGE,"E96"),sQuery(id+"F1.wireOp",EDGE,"E97"),sQuery(id+"F1.wireOp",EDGE,"E98"),sQuery(id+"F1.wireOp",EDGE,"E99"),sQuery(id+"F1.wireOp",EDGE,"E100"),sQuery(id+"F1.wireOp",EDGE,"E101"),sQuery(id+"F1.wireOp",EDGE,"E102"),sQuery(id+"F1.wireOp",EDGE,"E103.trimOffspring")])],"isStart":true});
            var sketch = newSketch(context, id + "F24", { "sketchPlane" : qUnion([Q0])});
            skCircle(sketch, "E156", {"center": v(-73.77, 51.85) * mm, "radius": 1.75 * mm});
            skCircle(sketch, "E157", {"center": v(73.77, 51.85) * mm, "radius": 1.75 * mm});
            skSolve(sketch);
        }
        {
            var Q0;
            Q0=qSketchRegion(id+"F24",true);
            extrude(context, id + "F25", {"entities" : qUnion([Q0]), "operationType" : NewBodyOperationType.REMOVE, "endBound" : BoundingType.UP_TO_NEXT, "oppositeDirection" : true, "depth" : 25 * mm, "offsetDistance" : 25 * mm});
        }
        {
            var Q0;
            Q0=makeQuery(id+"F10.boolean.opBoolean","COPY",FACE,{"derivedFrom":makeQuery(id+"F10.opExtrude","SWEPT_FACE",FACE,{"disambiguationData":[OSD([sQuery(id+"F9.wireOp",EDGE,"E130")])]})});
            var sketch = newSketch(context, id + "F26", { "sketchPlane" : qUnion([Q0])});
            skLineSegment(sketch, "E158", {"start": v(12.3, 0.73) * mm, "end": v(16.3, 7.66) * mm, "construction": true});
            skLineSegment(sketch, "E159", {"start": v(16.3, 7.66) * mm, "end": v(20.3, 0.73) * mm, "construction": true});
            skLineSegment(sketch, "E160", {"start": v(20.3, 0.73) * mm, "end": v(24.3, 7.66) * mm, "construction": true});
            skLineSegment(sketch, "E161", {"start": v(24.3, 7.66) * mm, "end": v(16.3, 7.66) * mm, "construction": true});
            skLineSegment(sketch, "E162", {"start": v(8.3, 7.66) * mm, "end": v(12.3, 0.73) * mm, "construction": true});
            skLineSegment(sketch, "E163", {"start": v(8.3, 7.66) * mm, "end": v(16.3, 7.66) * mm, "construction": true});
            skLineSegment(sketch, "E164", {"start": v(12.3, 0.73) * mm, "end": v(20.3, 0.73) * mm, "construction": true});
            skCircle(sketch, "E165", {"center": v(8.3, 7.66) * mm, "radius": 2.5 * mm});
            skCircle(sketch, "E166", {"center": v(16.3, 7.66) * mm, "radius": 2.5 * mm});
            skCircle(sketch, "E167", {"center": v(24.3, 7.66) * mm, "radius": 2.5 * mm});
            skCircle(sketch, "E168", {"center": v(20.3, 0.73) * mm, "radius": 2.5 * mm});
            skCircle(sketch, "E169", {"center": v(12.3, 0.73) * mm, "radius": 2.5 * mm});
            skLineSegment(sketch, "E170", {"start": v(8.3, 7.66) * mm, "end": v(8.3, 16.9) * mm, "construction": true});
            skLineSegment(sketch, "E171", {"start": v(12.3, 0.73) * mm, "end": v(12.3, -8.51) * mm, "construction": true});
            skLineSegment(sketch, "E172", {"start": v(20.3, 0.73) * mm, "end": v(28.3, 0.73) * mm, "construction": true});
            skLineSegment(sketch, "E173", {"start": v(28.3, 0.73) * mm, "end": v(24.3, 7.66) * mm, "construction": true});
            skLineSegment(sketch, "E174", {"start": v(32.3, 7.66) * mm, "end": v(28.3, 0.73) * mm, "construction": true});
            skLineSegment(sketch, "E175", {"start": v(24.3, 7.66) * mm, "end": v(32.3, 7.66) * mm, "construction": true});
            skLineSegment(sketch, "E176", {"start": v(28.3, 0.73) * mm, "end": v(36.3, 0.73) * mm, "construction": true});
            skLineSegment(sketch, "E177", {"start": v(36.3, 0.73) * mm, "end": v(32.3, 7.66) * mm, "construction": true});
            skLineSegment(sketch, "E178", {"start": v(32.3, 7.66) * mm, "end": v(40.3, 7.66) * mm, "construction": true});
            skLineSegment(sketch, "E179", {"start": v(40.3, 7.66) * mm, "end": v(36.3, 0.73) * mm, "construction": true});
            skCircle(sketch, "E180", {"center": v(32.3, 7.66) * mm, "radius": 2.5 * mm});
            skCircle(sketch, "E181", {"center": v(28.3, 0.73) * mm, "radius": 2.5 * mm});
            skCircle(sketch, "E182", {"center": v(36.3, 0.73) * mm, "radius": 2.5 * mm});
            skCircle(sketch, "E183", {"center": v(40.3, 7.66) * mm, "radius": 2.5 * mm});
            skSolve(sketch);
        }
        {
            var Q0;
            Q0=qSketchRegion(id+"F26",true);
            extrude(context, id + "F27", {"entities" : qUnion([Q0]), "operationType" : NewBodyOperationType.REMOVE, "endBound" : BoundingType.UP_TO_NEXT, "oppositeDirection" : true, "depth" : 25 * mm, "offsetDistance" : 25 * mm});
        }
        {
            var Q0;
            {var subQ0=sQuery(id+"F6.wireOp",EDGE,"E125");Q0=makeQuery(id+"F8.boolean.opBoolean","MERGE",FACE,{"derivedFrom":[makeQuery(id+"F7.boolean.opBoolean","COPY",FACE,{"derivedFrom":makeQuery(id+"F7.opExtrude","SWEPT_FACE",FACE,{"disambiguationData":[OSD([subQ0])]})}),makeQuery(id+"F8.opExtrude","SWEPT_FACE",FACE,{"disambiguationData":[OSD([subQ0])]})]});}
            var sketch = newSketch(context, id + "F28", { "sketchPlane" : qUnion([Q0])});
            skPoint(sketch, "E184.startSnap0", {"position": v(3.5, -1.33) * mm});
            skLineSegment(sketch, "E185", {"start": v(-48, -3.27) * mm, "end": v(4, -3.27) * mm});
            skLineSegment(sketch, "E186", {"start": v(-38, -57.95) * mm, "end": v(-6, -57.95) * mm});
            skLineSegment(sketch, "E187", {"start": v(-48, -3.27) * mm, "end": v(-48, -47.95) * mm});
            skLineSegment(sketch, "E188", {"start": v(4, -3.27) * mm, "end": v(4, -47.95) * mm});
            skArc(sketch, "E189", {"start": v(-48, -47.95) * mm, "mid": v(-45.07, -55.02) * mm, "end": v(-38, -57.95) * mm});
            skArc(sketch, "E190", {"start": v(-6, -57.95) * mm, "mid": v(1.07, -55.02) * mm, "end": v(4, -47.95) * mm});
            skSolve(sketch);
        }
        {
            var Q0;
            Q0=qSketchRegion(id+"F28",true);
            extrude(context, id + "F29", {"entities" : qUnion([Q0]), "operationType" : NewBodyOperationType.REMOVE, "oppositeDirection" : true, "depth" : 1 * mm, "offsetDistance" : 25 * mm});
        }
        {
            var Q0;
            Q0=makeQuery(id+"F2.opExtrude","SWEPT_FACE",FACE,{"disambiguationData":[OSD([sQuery(id+"F1.wireOp",EDGE,"E92")])]});
            var sketch = newSketch(context, id + "F30", { "sketchPlane" : qUnion([Q0])});
            skLineSegment(sketch, "E191", {"start": v(-33.98, 32.82) * mm, "end": v(-25.98, 32.82) * mm, "construction": true});
            skLineSegment(sketch, "E192", {"start": v(-25.98, 32.82) * mm, "end": v(-29.98, 25.9) * mm, "construction": true});
            skLineSegment(sketch, "E193", {"start": v(-29.98, 25.9) * mm, "end": v(-33.98, 32.82) * mm, "construction": true});
            skLineSegment(sketch, "E194", {"start": v(-29.98, 25.9) * mm, "end": v(-21.98, 25.9) * mm, "construction": true});
            skLineSegment(sketch, "E195", {"start": v(-21.98, 25.9) * mm, "end": v(-25.98, 32.82) * mm, "construction": true});
            skLineSegment(sketch, "E196", {"start": v(-25.98, 32.82) * mm, "end": v(-17.98, 32.82) * mm, "construction": true});
            skLineSegment(sketch, "E197", {"start": v(-17.98, 32.82) * mm, "end": v(-21.98, 25.9) * mm, "construction": true});
            skLineSegment(sketch, "E198", {"start": v(-21.98, 25.9) * mm, "end": v(-13.98, 25.9) * mm, "construction": true});
            skLineSegment(sketch, "E199", {"start": v(-13.98, 25.9) * mm, "end": v(-17.98, 32.82) * mm, "construction": true});
            skLineSegment(sketch, "E200", {"start": v(-17.98, 32.82) * mm, "end": v(-9.98, 32.82) * mm, "construction": true});
            skLineSegment(sketch, "E201", {"start": v(-9.98, 32.82) * mm, "end": v(-13.98, 25.9) * mm, "construction": true});
            skCircle(sketch, "E202", {"center": v(-33.98, 32.82) * mm, "radius": 2.5 * mm});
            skCircle(sketch, "E203", {"center": v(-25.98, 32.82) * mm, "radius": 2.5 * mm});
            skCircle(sketch, "E204", {"center": v(-17.98, 32.82) * mm, "radius": 2.5 * mm});
            skCircle(sketch, "E205", {"center": v(-9.98, 32.82) * mm, "radius": 2.5 * mm});
            skCircle(sketch, "E206", {"center": v(-29.98, 25.9) * mm, "radius": 2.5 * mm});
            skCircle(sketch, "E207", {"center": v(-21.98, 25.9) * mm, "radius": 2.5 * mm});
            skCircle(sketch, "E208", {"center": v(-13.98, 25.9) * mm, "radius": 2.5 * mm});
            skLineSegment(sketch, "E209", {"start": v(-9.98, 32.82) * mm, "end": v(-0.3, 32.82) * mm, "construction": true});
            skLineSegment(sketch, "E210", {"start": v(-29.98, 25.9) * mm, "end": v(-33.98, 18.97) * mm, "construction": true});
            skLineSegment(sketch, "E211", {"start": v(-33.98, 18.97) * mm, "end": v(-25.98, 18.97) * mm, "construction": true});
            skLineSegment(sketch, "E212", {"start": v(-25.98, 18.97) * mm, "end": v(-29.98, 25.9) * mm, "construction": true});
            skLineSegment(sketch, "E213", {"start": v(-25.98, 18.97) * mm, "end": v(-21.98, 25.9) * mm, "construction": true});
            skLineSegment(sketch, "E214", {"start": v(-25.98, 18.97) * mm, "end": v(-17.98, 18.97) * mm, "construction": true});
            skLineSegment(sketch, "E215", {"start": v(-17.98, 18.97) * mm, "end": v(-21.98, 25.9) * mm, "construction": true});
            skLineSegment(sketch, "E216", {"start": v(-13.98, 25.9) * mm, "end": v(-17.98, 18.97) * mm, "construction": true});
            skLineSegment(sketch, "E217", {"start": v(-17.98, 18.97) * mm, "end": v(-9.98, 18.97) * mm, "construction": true});
            skLineSegment(sketch, "E218", {"start": v(-9.98, 18.97) * mm, "end": v(-13.98, 25.9) * mm, "construction": true});
            skCircle(sketch, "E219", {"center": v(-33.98, 18.97) * mm, "radius": 2.5 * mm});
            skCircle(sketch, "E220", {"center": v(-25.98, 18.97) * mm, "radius": 2.5 * mm});
            skCircle(sketch, "E221", {"center": v(-17.98, 18.97) * mm, "radius": 2.5 * mm});
            skCircle(sketch, "E222", {"center": v(-9.98, 18.97) * mm, "radius": 2.5 * mm});
            skLineSegment(sketch, "E223", {"start": v(-33.98, 32.82) * mm, "end": v(-43.65, 32.82) * mm, "construction": true});
            skLineSegment(sketch, "E224", {"start": v(-0.3, 41.91) * mm, "end": v(-0.3, 0) * mm, "construction": true});
            skPoint(sketch, "E225.orphan", {"position": v(0, 32.82) * mm});
            skSolve(sketch);
        }
        {
            var Q0;
            Q0=qSketchRegion(id+"F30",true);
            extrude(context, id + "F31", {"entities" : qUnion([Q0]), "operationType" : NewBodyOperationType.REMOVE, "endBound" : BoundingType.UP_TO_NEXT, "oppositeDirection" : true, "depth" : 25 * mm, "offsetDistance" : 25 * mm});
        }
        {
            var Q0;
            Q0=makeQuery(id+"F2.opExtrude","SWEPT_FACE",FACE,{"disambiguationData":[OSD([sQuery(id+"F1.wireOp",EDGE,"E95.trimOffspring")])]});
            var sketch = newSketch(context, id + "F32", { "sketchPlane" : qUnion([Q0])});
            skLineSegment(sketch, "E226.bottom", {"start": v(-36, 10) * mm, "end": v(36, 10) * mm});
            skLineSegment(sketch, "E226.top", {"start": v(-36, 0) * mm, "end": v(36, 0) * mm});
            skLineSegment(sketch, "E226.left", {"start": v(-36, 10) * mm, "end": v(-36, 0) * mm});
            skLineSegment(sketch, "E226.right", {"start": v(36, 10) * mm, "end": v(36, 0) * mm});
            skSolve(sketch);
        }
        {
            var Q0;
            Q0=qSketchRegion(id+"F32",true);
            var Q1;
            Q1=makeQuery(id+"F14.opShell","OFFSET_FACE",FACE,{"disambiguationData":[OSD([sQuery(id+"F1.wireOp",EDGE,"E95.trimOffspring"),sQuery(id+"F1.wireOp",EDGE,"E102")])]});
            extrude(context, id + "F33", {"entities" : qUnion([Q0]), "operationType" : NewBodyOperationType.REMOVE, "oppositeDirection" : true, "depth" : 3 * mm, "endBoundEntityFace" : qUnion([Q1]), "offsetDistance" : 25 * mm});
        }
        {
            var Q0;
            Q0=makeQuery(id+"F33.boolean.opBoolean","COPY",EDGE,{"derivedFrom":makeQuery(id+"F33.opExtrude","SWEPT_EDGE",EDGE,{"disambiguationData":[OSD([sQuery(id+"F32.wireOp",EDGE,"E226.bottom"),sQuery(id+"F32.wireOp",EDGE,"E226.left")])]})});
            var Q1;
            Q1=makeQuery(id+"F33.boolean.opBoolean","COPY",EDGE,{"derivedFrom":makeQuery(id+"F33.opExtrude","SWEPT_EDGE",EDGE,{"disambiguationData":[OSD([sQuery(id+"F32.wireOp",EDGE,"E226.bottom"),sQuery(id+"F32.wireOp",EDGE,"E226.right")])]})});
            fillet(context, id + "F34", {"entities" : qUnion([Q0, Q1]), "radius" : 5 * mm, "tangentPropagation" : true, "allowEdgeOverflow" : false});
        }
        {
            var Q0;
            {var subQ0=sQuery(id+"F6.wireOp",EDGE,"E125");Q0=makeQuery(id+"F8.boolean.opBoolean","MERGE",FACE,{"derivedFrom":[makeQuery(id+"F7.boolean.opBoolean","COPY",FACE,{"derivedFrom":makeQuery(id+"F7.opExtrude","SWEPT_FACE",FACE,{"disambiguationData":[OSD([subQ0])]})}),makeQuery(id+"F8.opExtrude","SWEPT_FACE",FACE,{"disambiguationData":[OSD([subQ0])]})]});}
            var sketch = newSketch(context, id + "F35", { "sketchPlane" : qUnion([Q0])});
            skLineSegment(sketch, "E227", {"start": v(8.5, -3.27) * mm, "end": v(8.5, -38.73) * mm});
            skLineSegment(sketch, "E228", {"start": v(8.5, -38.73) * mm, "end": v(18.5, -60.73) * mm});
            skLineSegment(sketch, "E229", {"start": v(18.5, -60.73) * mm, "end": v(48.5, -60.73) * mm});
            skLineSegment(sketch, "E230", {"start": v(48.5, -60.73) * mm, "end": v(58.5, -38.73) * mm});
            skLineSegment(sketch, "E231", {"start": v(58.5, -38.73) * mm, "end": v(58.5, -3.27) * mm});
            skLineSegment(sketch, "E232", {"start": v(8.5, -3.27) * mm, "end": v(58.5, -3.27) * mm});
            skSolve(sketch);
        }
        {
            var Q0;
            Q0=qSketchRegion(id+"F35",true);
            extrude(context, id + "F36", {"entities" : qUnion([Q0]), "operationType" : NewBodyOperationType.REMOVE, "oppositeDirection" : true, "depth" : 1 * mm, "offsetDistance" : 25 * mm});
        }
        {
            var Q0;
            Q0=makeQuery(id+"F10.boolean.opBoolean","COPY",FACE,{"derivedFrom":makeQuery(id+"F10.opExtrude","SWEPT_FACE",FACE,{"disambiguationData":[OSD([sQuery(id+"F9.wireOp",EDGE,"E129")])]})});
            var sketch = newSketch(context, id + "F37", { "sketchPlane" : qUnion([Q0])});
            skLineSegment(sketch, "E233", {"start": v(-4.9, -5.3) * mm, "end": v(-17.16, -5.3) * mm});
            skLineSegment(sketch, "E234", {"start": v(-17.16, -5.3) * mm, "end": v(-17.16, -44.87) * mm});
            skLineSegment(sketch, "E235", {"start": v(-4.9, -5.3) * mm, "end": v(-4.9, -12.36) * mm});
            skLineSegment(sketch, "E236", {"start": v(-4.9, -12.36) * mm, "end": v(-14.68, -49.8) * mm});
            skLineSegment(sketch, "E237", {"start": v(-17.16, -44.87) * mm, "end": v(-14.68, -49.8) * mm});
            skSolve(sketch);
        }
        {
            var Q0;
            Q0=qSketchRegion(id+"F37",true);
            extrude(context, id + "F38", {"entities" : qUnion([Q0]), "operationType" : NewBodyOperationType.REMOVE, "oppositeDirection" : true, "depth" : 1 * mm, "offsetDistance" : 25 * mm});
        }
        {
            var Q0;
            Q0=makeQuery(id+"F38.boolean.opBoolean","COPY",EDGE,{"derivedFrom":makeQuery(id+"F38.opExtrude","SWEPT_EDGE",EDGE,{"disambiguationData":[OSD([sQuery(id+"F37.wireOp",EDGE,"E233"),sQuery(id+"F37.wireOp",EDGE,"E235")])]})});
            var Q1;
            Q1=makeQuery(id+"F38.boolean.opBoolean","COPY",EDGE,{"derivedFrom":makeQuery(id+"F38.opExtrude","SWEPT_EDGE",EDGE,{"disambiguationData":[OSD([sQuery(id+"F37.wireOp",EDGE,"E235"),sQuery(id+"F37.wireOp",EDGE,"E236")])]})});
            var Q2;
            Q2=makeQuery(id+"F38.boolean.opBoolean","COPY",EDGE,{"derivedFrom":makeQuery(id+"F38.opExtrude","SWEPT_EDGE",EDGE,{"disambiguationData":[OSD([sQuery(id+"F37.wireOp",EDGE,"E233"),sQuery(id+"F37.wireOp",EDGE,"E234")])]})});
            var Q3;
            Q3=makeQuery(id+"F38.boolean.opBoolean","COPY",EDGE,{"derivedFrom":makeQuery(id+"F38.opExtrude","SWEPT_EDGE",EDGE,{"disambiguationData":[OSD([sQuery(id+"F37.wireOp",EDGE,"E234"),sQuery(id+"F37.wireOp",EDGE,"E237")])]})});
            fillet(context, id + "F39", {"entities" : qUnion([Q0, Q1, Q2, Q3]), "radius" : 3 * mm, "tangentPropagation" : true, "allowEdgeOverflow" : false});
        }
        {
            var Q0;
            Q0=makeQuery(id+"F7.boolean.opBoolean","COPY",FACE,{"derivedFrom":makeQuery(id+"F7.opExtrude","SWEPT_FACE",FACE,{"disambiguationData":[OSD([sQuery(id+"F6.wireOp",EDGE,"E126")])]})});
            var sketch = newSketch(context, id + "F40", { "sketchPlane" : qUnion([Q0])});
            skLineSegment(sketch, "E238", {"start": v(5, -11.4) * mm, "end": v(51.16, -11.4) * mm});
            skLineSegment(sketch, "E239", {"start": v(5, -11.4) * mm, "end": v(5, 11.47) * mm});
            skLineSegment(sketch, "E240", {"start": v(5, 11.47) * mm, "end": v(53.98, 11.47) * mm});
            skLineSegment(sketch, "E241", {"start": v(51.16, -11.4) * mm, "end": v(53.98, 11.47) * mm});
            skLineSegment(sketch, "E242", {"start": v(5, -11.4) * mm, "end": v(21.6, 11.47) * mm, "construction": true});
            skLineSegment(sketch, "E243", {"start": v(53.98, 11.47) * mm, "end": v(37.37, -11.4) * mm, "construction": true});
            skLineSegment(sketch, "E244", {"start": v(21.19, -11.4) * mm, "end": v(37.8, 11.47) * mm, "construction": true});
            skLineSegment(sketch, "E245", {"start": v(21.19, -11.4) * mm, "end": v(10.6, -3.7) * mm, "construction": true});
            skLineSegment(sketch, "E246", {"start": v(37.8, 11.47) * mm, "end": v(48.4, 3.77) * mm, "construction": true});
            skLineSegment(sketch, "E247", {"start": v(19.03, 7.92) * mm, "end": v(8.86, -6.08) * mm});
            skLineSegment(sketch, "E248", {"start": v(21.46, 6.15) * mm, "end": v(11.29, -7.85) * mm});
            skLineSegment(sketch, "E249", {"start": v(33.36, 7.92) * mm, "end": v(23.2, -6.08) * mm});
            skLineSegment(sketch, "E250", {"start": v(25.62, -7.85) * mm, "end": v(35.8, 6.15) * mm});
            skLineSegment(sketch, "E251", {"start": v(50.12, 6.15) * mm, "end": v(39.95, -7.85) * mm});
            skLineSegment(sketch, "E252", {"start": v(37.53, -6.08) * mm, "end": v(47.7, 7.92) * mm});
            skArc(sketch, "E253", {"start": v(21.46, 6.15) * mm, "mid": v(21.13, 8.25) * mm, "end": v(19.03, 7.92) * mm});
            skArc(sketch, "E254", {"start": v(8.86, -6.08) * mm, "mid": v(9.2, -8.18) * mm, "end": v(11.29, -7.85) * mm});
            skArc(sketch, "E255", {"start": v(35.8, 6.15) * mm, "mid": v(35.46, 8.25) * mm, "end": v(33.36, 7.92) * mm});
            skArc(sketch, "E256", {"start": v(23.2, -6.08) * mm, "mid": v(23.52, -8.18) * mm, "end": v(25.62, -7.85) * mm});
            skArc(sketch, "E257", {"start": v(37.53, -6.08) * mm, "mid": v(37.86, -8.18) * mm, "end": v(39.95, -7.85) * mm});
            skArc(sketch, "E258", {"start": v(50.12, 6.15) * mm, "mid": v(49.8, 8.25) * mm, "end": v(47.7, 7.92) * mm});
            skLineSegment(sketch, "E259", {"start": v(5, 0.03) * mm, "end": v(52.57, 0.03) * mm, "construction": true});
            skLineSegment(sketch, "E260", {"start": v(20.24, 7.03) * mm, "end": v(48.91, 7.03) * mm, "construction": true});
            skLineSegment(sketch, "E261", {"start": v(10.07, -6.97) * mm, "end": v(38.74, -6.97) * mm, "construction": true});
            skLineSegment(sketch, "E262", {"start": v(-42, 11.47) * mm, "end": v(-42, -11.4) * mm});
            skLineSegment(sketch, "E263", {"start": v(-42, -11.4) * mm, "end": v(-51.16, -11.4) * mm});
            skLineSegment(sketch, "E264", {"start": v(-51.16, -11.4) * mm, "end": v(-53.98, 11.47) * mm});
            skLineSegment(sketch, "E265", {"start": v(-53.98, 11.47) * mm, "end": v(-42, 11.47) * mm});
            skSolve(sketch);
        }
        {
            var Q0;
            Q0=qSketchRegion(id+"F40",true);
            extrude(context, id + "F41", {"entities" : qUnion([Q0]), "operationType" : NewBodyOperationType.REMOVE, "oppositeDirection" : true, "depth" : 1 * mm, "offsetDistance" : 25 * mm});
        }
        {
            var Q0;
            Q0=makeQuery(id+"F41.boolean.opBoolean","COPY",EDGE,{"derivedFrom":makeQuery(id+"F41.opExtrude","SWEPT_EDGE",EDGE,{"disambiguationData":[OSD([sQuery(id+"F40.wireOp",EDGE,"E239"),sQuery(id+"F40.wireOp",EDGE,"E240")])]})});
            var Q1;
            Q1=makeQuery(id+"F41.boolean.opBoolean","COPY",EDGE,{"derivedFrom":makeQuery(id+"F41.opExtrude","SWEPT_EDGE",EDGE,{"disambiguationData":[OSD([sQuery(id+"F40.wireOp",EDGE,"E240"),sQuery(id+"F40.wireOp",EDGE,"E241")])]})});
            var Q2;
            Q2=makeQuery(id+"F41.boolean.opBoolean","COPY",EDGE,{"derivedFrom":makeQuery(id+"F41.opExtrude","SWEPT_EDGE",EDGE,{"disambiguationData":[OSD([sQuery(id+"F40.wireOp",EDGE,"E238"),sQuery(id+"F40.wireOp",EDGE,"E239")])]})});
            var Q3;
            Q3=makeQuery(id+"F41.boolean.opBoolean","COPY",EDGE,{"derivedFrom":makeQuery(id+"F41.opExtrude","SWEPT_EDGE",EDGE,{"disambiguationData":[OSD([sQuery(id+"F40.wireOp",EDGE,"E238"),sQuery(id+"F40.wireOp",EDGE,"E241")])]})});
            fillet(context, id + "F42", {"entities" : qUnion([Q0, Q1, Q2, Q3]), "radius" : 5 * mm, "tangentPropagation" : true, "allowEdgeOverflow" : false});
        }
        {
            var Q0;
            Q0=makeQuery(id+"F41.boolean.opBoolean","COPY",EDGE,{"derivedFrom":makeQuery(id+"F41.opExtrude","SWEPT_EDGE",EDGE,{"disambiguationData":[OSD([sQuery(id+"F40.wireOp",EDGE,"E263"),sQuery(id+"F40.wireOp",EDGE,"E264")])]})});
            var Q1;
            Q1=makeQuery(id+"F41.boolean.opBoolean","COPY",EDGE,{"derivedFrom":makeQuery(id+"F41.opExtrude","SWEPT_EDGE",EDGE,{"disambiguationData":[OSD([sQuery(id+"F40.wireOp",EDGE,"E262"),sQuery(id+"F40.wireOp",EDGE,"E263")])]})});
            var Q2;
            Q2=makeQuery(id+"F41.boolean.opBoolean","COPY",EDGE,{"derivedFrom":makeQuery(id+"F41.opExtrude","SWEPT_EDGE",EDGE,{"disambiguationData":[OSD([sQuery(id+"F40.wireOp",EDGE,"E264"),sQuery(id+"F40.wireOp",EDGE,"E265")])]})});
            var Q3;
            Q3=makeQuery(id+"F41.boolean.opBoolean","COPY",EDGE,{"derivedFrom":makeQuery(id+"F41.opExtrude","SWEPT_EDGE",EDGE,{"disambiguationData":[OSD([sQuery(id+"F40.wireOp",EDGE,"E262"),sQuery(id+"F40.wireOp",EDGE,"E265")])]})});
            fillet(context, id + "F43", {"entities" : qUnion([Q0, Q1, Q2, Q3]), "radius" : 3 * mm, "tangentPropagation" : true, "allowEdgeOverflow" : false});
        }
        {
            var Q0;
            Q0=makeQuery(id+"F12.boolean.opBoolean","MERGE",FACE,{"derivedFrom":[makeQuery(id+"F2.opExtrude","SWEPT_FACE",FACE,{"disambiguationData":[OSD([sQuery(id+"F1.wireOp",EDGE,"E93")])]}),makeQuery(id+"F12.opExtrude","SWEPT_FACE",FACE,{"disambiguationData":[OSD([sQuery(id+"F11.wireOp",EDGE,"E145")])]})]});
            var sketch = newSketch(context, id + "F44", { "sketchPlane" : qUnion([Q0])});
            skLineSegment(sketch, "E266", {"start": v(27.88, 7) * mm, "end": v(53.13, 7) * mm});
            skLineSegment(sketch, "E267", {"start": v(53.13, 7) * mm, "end": v(53.13, 21.36) * mm});
            skLineSegment(sketch, "E268", {"start": v(53.13, 21.36) * mm, "end": v(46.93, 37.9) * mm});
            skLineSegment(sketch, "E269", {"start": v(46.93, 37.9) * mm, "end": v(27.88, 31.85) * mm});
            skLineSegment(sketch, "E270", {"start": v(27.88, 31.85) * mm, "end": v(27.88, 7) * mm});
            skLineSegment(sketch, "E271", {"start": v(27.88, 31.85) * mm, "end": v(53.13, 21.36) * mm, "construction": true});
            skLineSegment(sketch, "E272", {"start": v(53.13, 9) * mm, "end": v(27.88, 19.49) * mm, "construction": true});
            skLineSegment(sketch, "E273", {"start": v(33.46, 29.53) * mm, "end": v(48.7, 23.2) * mm});
            skLineSegment(sketch, "E274", {"start": v(32.3, 26.76) * mm, "end": v(47.55, 20.42) * mm});
            skLineSegment(sketch, "E275", {"start": v(32.3, 17.65) * mm, "end": v(47.55, 11.32) * mm});
            skArc(sketch, "E276", {"start": v(33.46, 29.53) * mm, "mid": v(31.5, 28.72) * mm, "end": v(32.3, 26.76) * mm});
            skArc(sketch, "E277", {"start": v(47.55, 20.42) * mm, "mid": v(49.52, 21.23) * mm, "end": v(48.7, 23.2) * mm});
            skArc(sketch, "E278", {"start": v(33.46, 20.42) * mm, "mid": v(31.5, 19.61) * mm, "end": v(32.3, 17.65) * mm});
            skLineSegment(sketch, "E279", {"start": v(33.46, 20.42) * mm, "end": v(48.7, 14.09) * mm});
            skArc(sketch, "E280", {"start": v(47.55, 11.32) * mm, "mid": v(49.52, 12.13) * mm, "end": v(48.7, 14.09) * mm});
            skSolve(sketch);
        }
        {
            var Q0;
            Q0=qSketchRegion(id+"F44",true);
            extrude(context, id + "F45", {"entities" : qUnion([Q0]), "operationType" : NewBodyOperationType.REMOVE, "oppositeDirection" : true, "depth" : 1 * mm, "offsetDistance" : 25 * mm});
        }
        {
            var Q0;
            Q0=makeQuery(id+"F45.boolean.opBoolean","COPY",EDGE,{"derivedFrom":makeQuery(id+"F45.opExtrude","SWEPT_EDGE",EDGE,{"disambiguationData":[OSD([sQuery(id+"F44.wireOp",EDGE,"E269"),sQuery(id+"F44.wireOp",EDGE,"E270")])]})});
            var Q1;
            Q1=makeQuery(id+"F45.boolean.opBoolean","COPY",EDGE,{"derivedFrom":makeQuery(id+"F45.opExtrude","SWEPT_EDGE",EDGE,{"disambiguationData":[OSD([sQuery(id+"F44.wireOp",EDGE,"E268"),sQuery(id+"F44.wireOp",EDGE,"E269")])]})});
            var Q2;
            Q2=makeQuery(id+"F45.boolean.opBoolean","COPY",EDGE,{"derivedFrom":makeQuery(id+"F45.opExtrude","SWEPT_EDGE",EDGE,{"disambiguationData":[OSD([sQuery(id+"F44.wireOp",EDGE,"E267"),sQuery(id+"F44.wireOp",EDGE,"E268")])]})});
            var Q3;
            Q3=makeQuery(id+"F45.boolean.opBoolean","COPY",EDGE,{"derivedFrom":makeQuery(id+"F45.opExtrude","SWEPT_EDGE",EDGE,{"disambiguationData":[OSD([sQuery(id+"F44.wireOp",EDGE,"E266"),sQuery(id+"F44.wireOp",EDGE,"E267")])]})});
            var Q4;
            Q4=makeQuery(id+"F45.boolean.opBoolean","COPY",EDGE,{"derivedFrom":makeQuery(id+"F45.opExtrude","SWEPT_EDGE",EDGE,{"disambiguationData":[OSD([sQuery(id+"F44.wireOp",EDGE,"E266"),sQuery(id+"F44.wireOp",EDGE,"E270")])]})});
            fillet(context, id + "F46", {"entities" : qUnion([Q0, Q1, Q2, Q3, Q4]), "radius" : 5 * mm, "tangentPropagation" : true, "allowEdgeOverflow" : false});
        }
        {
            var Q0;
            Q0=makeQuery(id+"F12.boolean.opBoolean","MERGE",FACE,{"derivedFrom":[makeQuery(id+"F2.opExtrude","SWEPT_FACE",FACE,{"disambiguationData":[OSD([sQuery(id+"F1.wireOp",EDGE,"E94")])]}),makeQuery(id+"F12.opExtrude","SWEPT_FACE",FACE,{"disambiguationData":[OSD([sQuery(id+"F11.wireOp",EDGE,"E141")])]})]});
            var sketch = newSketch(context, id + "F47", { "sketchPlane" : qUnion([Q0])});
            skLineSegment(sketch, "E281", {"start": v(-47.12, 37.38) * mm, "end": v(-53.13, 21.36) * mm});
            skLineSegment(sketch, "E282", {"start": v(-27.88, 7) * mm, "end": v(-27.88, 40.55) * mm});
            skLineSegment(sketch, "E283", {"start": v(-27.88, 40.55) * mm, "end": v(-47.12, 37.38) * mm});
            skLineSegment(sketch, "E284", {"start": v(-53.13, 21.36) * mm, "end": v(-53.13, 7) * mm});
            skLineSegment(sketch, "E285", {"start": v(-27.88, 7) * mm, "end": v(-53.13, 7) * mm});
            skLineSegment(sketch, "E286", {"start": v(-27.88, 40.55) * mm, "end": v(-53.13, 21.36) * mm, "construction": true});
            skLineSegment(sketch, "E287", {"start": v(-53.13, 7) * mm, "end": v(-27.88, 26.2) * mm, "construction": true});
            skLineSegment(sketch, "E288", {"start": v(-46.57, 28.23) * mm, "end": v(-37.3, 35.27) * mm});
            skLineSegment(sketch, "E289", {"start": v(-44.75, 25.84) * mm, "end": v(-35.49, 32.88) * mm});
            skLineSegment(sketch, "E290", {"start": v(-47.46, 13.2) * mm, "end": v(-33.79, 23.59) * mm});
            skLineSegment(sketch, "E291", {"start": v(-45.65, 10.8) * mm, "end": v(-31.97, 21.2) * mm});
            skArc(sketch, "E292", {"start": v(-46.57, 28.23) * mm, "mid": v(-46.85, 26.13) * mm, "end": v(-44.75, 25.84) * mm});
            skArc(sketch, "E293", {"start": v(-35.49, 32.88) * mm, "mid": v(-35.2, 34.99) * mm, "end": v(-37.3, 35.27) * mm});
            skArc(sketch, "E294", {"start": v(-31.97, 21.2) * mm, "mid": v(-31.69, 23.3) * mm, "end": v(-33.79, 23.59) * mm});
            skArc(sketch, "E295", {"start": v(-47.46, 13.2) * mm, "mid": v(-47.75, 11.1) * mm, "end": v(-45.65, 10.8) * mm});
            skSolve(sketch);
        }
        {
            var Q0;
            Q0=qSketchRegion(id+"F47",true);
            extrude(context, id + "F48", {"entities" : qUnion([Q0]), "operationType" : NewBodyOperationType.REMOVE, "oppositeDirection" : true, "depth" : 1 * mm, "offsetDistance" : 25 * mm});
        }
        {
            var Q0;
            Q0=makeQuery(id+"F48.boolean.opBoolean","COPY",EDGE,{"derivedFrom":makeQuery(id+"F48.opExtrude","SWEPT_EDGE",EDGE,{"disambiguationData":[OSD([sQuery(id+"F47.wireOp",EDGE,"E281"),sQuery(id+"F47.wireOp",EDGE,"E283")])]})});
            var Q1;
            Q1=makeQuery(id+"F48.boolean.opBoolean","COPY",EDGE,{"derivedFrom":makeQuery(id+"F48.opExtrude","SWEPT_EDGE",EDGE,{"disambiguationData":[OSD([sQuery(id+"F47.wireOp",EDGE,"E282"),sQuery(id+"F47.wireOp",EDGE,"E283")])]})});
            var Q2;
            Q2=makeQuery(id+"F48.boolean.opBoolean","COPY",EDGE,{"derivedFrom":makeQuery(id+"F48.opExtrude","SWEPT_EDGE",EDGE,{"disambiguationData":[OSD([sQuery(id+"F47.wireOp",EDGE,"E281"),sQuery(id+"F47.wireOp",EDGE,"E284")])]})});
            var Q3;
            Q3=makeQuery(id+"F48.boolean.opBoolean","COPY",EDGE,{"derivedFrom":makeQuery(id+"F48.opExtrude","SWEPT_EDGE",EDGE,{"disambiguationData":[OSD([sQuery(id+"F47.wireOp",EDGE,"E284"),sQuery(id+"F47.wireOp",EDGE,"E285")])]})});
            var Q4;
            Q4=makeQuery(id+"F48.boolean.opBoolean","COPY",EDGE,{"derivedFrom":makeQuery(id+"F48.opExtrude","SWEPT_EDGE",EDGE,{"disambiguationData":[OSD([sQuery(id+"F47.wireOp",EDGE,"E282"),sQuery(id+"F47.wireOp",EDGE,"E285")])]})});
            fillet(context, id + "F49", {"entities" : qUnion([Q0, Q1, Q2, Q3, Q4]), "radius" : 5 * mm, "tangentPropagation" : true, "allowEdgeOverflow" : false});
        }
        {
            var Q0;
            Q0=makeQuery(id+"F38.boolean.opBoolean","COPY",EDGE,{"derivedFrom":makeQuery(id+"F38.opExtrude","CAP_EDGE",EDGE,{"disambiguationData":[OSD([sQuery(id+"F37.wireOp",EDGE,"E234")])],"isStart":false})});
            var Q1;
            Q1=makeQuery(id+"F38.boolean.opBoolean","COPY",EDGE,{"derivedFrom":makeQuery(id+"F38.opExtrude","CAP_EDGE",EDGE,{"disambiguationData":[OSD([sQuery(id+"F37.wireOp",EDGE,"E233")])],"isStart":false})});
            var Q2;
            Q2=makeQuery(id+"F38.boolean.opBoolean","COPY",EDGE,{"derivedFrom":makeQuery(id+"F38.opExtrude","CAP_EDGE",EDGE,{"disambiguationData":[OSD([sQuery(id+"F37.wireOp",EDGE,"E235")])],"isStart":false})});
            var Q3;
            Q3=makeQuery(id+"F38.boolean.opBoolean","COPY",EDGE,{"derivedFrom":makeQuery(id+"F38.opExtrude","CAP_EDGE",EDGE,{"disambiguationData":[OSD([sQuery(id+"F37.wireOp",EDGE,"E236")])],"isStart":false})});
            var Q4;
            Q4=makeQuery(id+"F38.boolean.opBoolean","COPY",EDGE,{"derivedFrom":makeQuery(id+"F38.opExtrude","CAP_EDGE",EDGE,{"disambiguationData":[OSD([sQuery(id+"F37.wireOp",EDGE,"E237")])],"isStart":false})});
            var Q5;
            Q5=makeQuery(id+"F41.boolean.opBoolean","COPY",EDGE,{"derivedFrom":makeQuery(id+"F41.opExtrude","CAP_EDGE",EDGE,{"disambiguationData":[OSD([sQuery(id+"F40.wireOp",EDGE,"E240")])],"isStart":false})});
            var Q6;
            Q6=makeQuery(id+"F41.boolean.opBoolean","COPY",EDGE,{"derivedFrom":makeQuery(id+"F41.opExtrude","CAP_EDGE",EDGE,{"disambiguationData":[OSD([sQuery(id+"F40.wireOp",EDGE,"E248")])],"isStart":false})});
            var Q7;
            Q7=makeQuery(id+"F41.boolean.opBoolean","COPY",EDGE,{"derivedFrom":makeQuery(id+"F41.opExtrude","CAP_EDGE",EDGE,{"disambiguationData":[OSD([sQuery(id+"F40.wireOp",EDGE,"E250")])],"isStart":false})});
            var Q8;
            Q8=makeQuery(id+"F41.boolean.opBoolean","COPY",EDGE,{"derivedFrom":makeQuery(id+"F41.opExtrude","CAP_EDGE",EDGE,{"disambiguationData":[OSD([sQuery(id+"F40.wireOp",EDGE,"E251")])],"isStart":false})});
            var Q9;
            Q9=makeQuery(id+"F41.boolean.opBoolean","COPY",EDGE,{"derivedFrom":makeQuery(id+"F41.opExtrude","CAP_EDGE",EDGE,{"disambiguationData":[OSD([sQuery(id+"F40.wireOp",EDGE,"E264")])],"isStart":false})});
            var Q10;
            Q10=makeQuery(id+"F45.boolean.opBoolean","COPY",EDGE,{"derivedFrom":makeQuery(id+"F45.opExtrude","CAP_EDGE",EDGE,{"disambiguationData":[OSD([sQuery(id+"F44.wireOp",EDGE,"E269")])],"isStart":false})});
            var Q11;
            Q11=makeQuery(id+"F45.boolean.opBoolean","COPY",EDGE,{"derivedFrom":makeQuery(id+"F45.opExtrude","CAP_EDGE",EDGE,{"disambiguationData":[OSD([sQuery(id+"F44.wireOp",EDGE,"E276")])],"isStart":false})});
            var Q12;
            Q12=makeQuery(id+"F45.boolean.opBoolean","COPY",EDGE,{"derivedFrom":makeQuery(id+"F45.opExtrude","CAP_EDGE",EDGE,{"disambiguationData":[OSD([sQuery(id+"F44.wireOp",EDGE,"E278")])],"isStart":false})});
            var Q13;
            Q13=makeQuery(id+"F48.boolean.opBoolean","COPY",EDGE,{"derivedFrom":makeQuery(id+"F48.opExtrude","CAP_EDGE",EDGE,{"disambiguationData":[OSD([sQuery(id+"F47.wireOp",EDGE,"E281")])],"isStart":false})});
            var Q14;
            Q14=makeQuery(id+"F48.boolean.opBoolean","COPY",EDGE,{"derivedFrom":makeQuery(id+"F48.opExtrude","CAP_EDGE",EDGE,{"disambiguationData":[OSD([sQuery(id+"F47.wireOp",EDGE,"E292")])],"isStart":false})});
            var Q15;
            Q15=makeQuery(id+"F48.boolean.opBoolean","COPY",EDGE,{"derivedFrom":makeQuery(id+"F48.opExtrude","CAP_EDGE",EDGE,{"disambiguationData":[OSD([sQuery(id+"F47.wireOp",EDGE,"E295")])],"isStart":false})});
            chamfer(context, id + "F50", {"entities" : qUnion([Q0, Q1, Q2, Q3, Q4, Q5, Q6, Q7, Q8, Q9, Q10, Q11, Q12, Q13, Q14, Q15]), "width" : 1 * mm, "tangentPropagation" : true});
        }
        {
            var Q0;
            {var subQ2=sQuery(id+"F1.wireOp",EDGE,"E90");var subQ3=makeQuery(id+"F2.opExtrude","SWEPT_FACE",FACE,{"disambiguationData":[OSD([subQ2])]});var subQ4=sQuery(id+"F1.wireOp",EDGE,"E91");var subQ5=sQuery(id+"F1.wireOp",EDGE,"E92");Q0=makeQuery(id+"F19.boolean.opBoolean","SPLIT",FACE,{"disambiguationData":[TD([makeQuery(id+"F10.boolean.opBoolean","COPY",FACE,{"derivedFrom":makeQuery(id+"F10.opExtrude","SWEPT_FACE",FACE,{"disambiguationData":[OSD([sQuery(id+"F9.wireOp",EDGE,"E129")])]})})])],"derivedFrom":makeQuery(id+"F7.boolean.opBoolean","SPLIT",FACE,{"disambiguationData":[TD([subQ3])],"derivedFrom":makeQuery(id+"F2.opExtrude","CAP_FACE",FACE,{"disambiguationData":[OSD([subQ2,subQ4,subQ5,sQuery(id+"F1.wireOp",EDGE,"E93"),sQuery(id+"F1.wireOp",EDGE,"E94"),sQuery(id+"F1.wireOp",EDGE,"E95.trimOffspring"),sQuery(id+"F1.wireOp",EDGE,"E96"),sQuery(id+"F1.wireOp",EDGE,"E97"),sQuery(id+"F1.wireOp",EDGE,"E98"),sQuery(id+"F1.wireOp",EDGE,"E99"),sQuery(id+"F1.wireOp",EDGE,"E100"),sQuery(id+"F1.wireOp",EDGE,"E101"),sQuery(id+"F1.wireOp",EDGE,"E102"),sQuery(id+"F1.wireOp",EDGE,"E103.trimOffspring")])],"isStart":false})})});}
            var sketch = newSketch(context, id + "F51", { "sketchPlane" : qUnion([Q0])});
            skLineSegment(sketch, "E296.bottom", {"start": v(-74.5, 0) * mm, "end": v(74.5, 0) * mm});
            skLineSegment(sketch, "E296.top", {"start": v(-74.5, -0.3) * mm, "end": v(74.5, -0.3) * mm});
            skLineSegment(sketch, "E296.left", {"start": v(-74.5, 0) * mm, "end": v(-74.5, -0.3) * mm});
            skLineSegment(sketch, "E296.right", {"start": v(74.5, 0) * mm, "end": v(74.5, -0.3) * mm});
            skSolve(sketch);
        }
        {
            var Q0;
            Q0=qSketchRegion(id+"F51",true);
            var Q1;
            {var subQ0=sQuery(id+"F1.wireOp",EDGE,"E98");var subQ1=sQuery(id+"F1.wireOp",EDGE,"E93");var subQ2=sQuery(id+"F1.wireOp",EDGE,"E95.trimOffspring");var subQ3=sQuery(id+"F1.wireOp",EDGE,"E97");var subQ4=sQuery(id+"F1.wireOp",EDGE,"E91");var subQ6=sQuery(id+"F1.wireOp",EDGE,"E96");var subQ7=sQuery(id+"F1.wireOp",EDGE,"E90");Q1=makeQuery(id+"F33.boolean.opBoolean","SPLIT",FACE,{"disambiguationData":[TD([makeQuery(id+"F2.opExtrude","SWEPT_FACE",FACE,{"disambiguationData":[OSD([subQ4])]})])],"derivedFrom":makeQuery(id+"F2.opExtrude","CAP_FACE",FACE,{"disambiguationData":[OSD([subQ7,subQ4,sQuery(id+"F1.wireOp",EDGE,"E92"),subQ1,sQuery(id+"F1.wireOp",EDGE,"E94"),subQ2,subQ6,subQ3,subQ0,sQuery(id+"F1.wireOp",EDGE,"E99"),sQuery(id+"F1.wireOp",EDGE,"E100"),sQuery(id+"F1.wireOp",EDGE,"E101"),sQuery(id+"F1.wireOp",EDGE,"E102"),sQuery(id+"F1.wireOp",EDGE,"E103.trimOffspring")])],"isStart":true})});}
            extrude(context, id + "F52", {"entities" : qUnion([Q0]), "operationType" : NewBodyOperationType.REMOVE, "endBound" : BoundingType.UP_TO_SURFACE, "oppositeDirection" : true, "depth" : 25 * mm, "endBoundEntityFace" : qUnion([Q1]), "offsetDistance" : 25 * mm});
        }
        {
            var Q0;
            {var subQ2=sQuery(id+"F1.wireOp",EDGE,"E90");var subQ3=makeQuery(id+"F2.opExtrude","SWEPT_FACE",FACE,{"disambiguationData":[OSD([subQ2])]});var subQ4=sQuery(id+"F1.wireOp",EDGE,"E91");var subQ5=sQuery(id+"F1.wireOp",EDGE,"E92");Q0=makeQuery(id+"F19.boolean.opBoolean","SPLIT",FACE,{"disambiguationData":[TD([makeQuery(id+"F10.boolean.opBoolean","COPY",FACE,{"derivedFrom":makeQuery(id+"F10.opExtrude","SWEPT_FACE",FACE,{"disambiguationData":[OSD([sQuery(id+"F9.wireOp",EDGE,"E129")])]})})])],"derivedFrom":makeQuery(id+"F7.boolean.opBoolean","SPLIT",FACE,{"disambiguationData":[TD([subQ3])],"derivedFrom":makeQuery(id+"F2.opExtrude","CAP_FACE",FACE,{"disambiguationData":[OSD([subQ2,subQ4,subQ5,sQuery(id+"F1.wireOp",EDGE,"E93"),sQuery(id+"F1.wireOp",EDGE,"E94"),sQuery(id+"F1.wireOp",EDGE,"E95.trimOffspring"),sQuery(id+"F1.wireOp",EDGE,"E96"),sQuery(id+"F1.wireOp",EDGE,"E97"),sQuery(id+"F1.wireOp",EDGE,"E98"),sQuery(id+"F1.wireOp",EDGE,"E99"),sQuery(id+"F1.wireOp",EDGE,"E100"),sQuery(id+"F1.wireOp",EDGE,"E101"),sQuery(id+"F1.wireOp",EDGE,"E102"),sQuery(id+"F1.wireOp",EDGE,"E103.trimOffspring")])],"isStart":false})})});}
            var sketch = newSketch(context, id + "F53", { "sketchPlane" : qUnion([Q0])});
            skLineSegment(sketch, "E297.bottom", {"start": v(13.5, -13) * mm, "end": v(8.5, -13) * mm});
            skLineSegment(sketch, "E297.top", {"start": v(13.5, -0.3) * mm, "end": v(11.5, -0.3) * mm});
            skLineSegment(sketch, "E297.left", {"start": v(13.5, -13) * mm, "end": v(13.5, -0.3) * mm});
            skLineSegment(sketch, "E298.bottom", {"start": v(53.5, -0.3) * mm, "end": v(55.5, -0.3) * mm});
            skLineSegment(sketch, "E298.top", {"start": v(53.5, -13) * mm, "end": v(58.5, -13) * mm});
            skLineSegment(sketch, "E298.left", {"start": v(53.5, -0.3) * mm, "end": v(53.5, -13) * mm});
            skLineSegment(sketch, "E299", {"start": v(11.5, -0.3) * mm, "end": v(11.5, -4.9) * mm});
            skLineSegment(sketch, "E300", {"start": v(8.5, -13) * mm, "end": v(8.5, -8.4) * mm});
            skLineSegment(sketch, "E301", {"start": v(8.5, -8.4) * mm, "end": v(11.5, -4.9) * mm});
            skLineSegment(sketch, "E302", {"start": v(58.5, -13) * mm, "end": v(58.5, -8.4) * mm});
            skLineSegment(sketch, "E303", {"start": v(55.5, -0.3) * mm, "end": v(55.5, -4.9) * mm});
            skLineSegment(sketch, "E304", {"start": v(55.5, -4.9) * mm, "end": v(58.5, -8.4) * mm});
            skSolve(sketch);
        }
        {
            var Q0;
            Q0=qSketchRegion(id+"F53",true);
            extrude(context, id + "F54", {"entities" : qUnion([Q0]), "operationType" : NewBodyOperationType.REMOVE, "oppositeDirection" : true, "depth" : 1 * mm, "offsetDistance" : 25 * mm});
        }
        {
            var Q0;
            Q0=makeQuery(id+"F54.boolean.opBoolean","COPY",EDGE,{"derivedFrom":makeQuery(id+"F54.opExtrude","SWEPT_EDGE",EDGE,{"disambiguationData":[OSD([sQuery(id+"F53.wireOp",EDGE,"E299"),sQuery(id+"F53.wireOp",EDGE,"E301")])]})});
            var Q1;
            Q1=makeQuery(id+"F54.boolean.opBoolean","COPY",EDGE,{"derivedFrom":makeQuery(id+"F54.opExtrude","SWEPT_EDGE",EDGE,{"disambiguationData":[OSD([sQuery(id+"F53.wireOp",EDGE,"E300"),sQuery(id+"F53.wireOp",EDGE,"E301")])]})});
            var Q2;
            Q2=makeQuery(id+"F54.boolean.opBoolean","COPY",EDGE,{"derivedFrom":makeQuery(id+"F54.opExtrude","SWEPT_EDGE",EDGE,{"disambiguationData":[OSD([sQuery(id+"F53.wireOp",EDGE,"E303"),sQuery(id+"F53.wireOp",EDGE,"E304")])]})});
            var Q3;
            Q3=makeQuery(id+"F54.boolean.opBoolean","COPY",EDGE,{"derivedFrom":makeQuery(id+"F54.opExtrude","SWEPT_EDGE",EDGE,{"disambiguationData":[OSD([sQuery(id+"F53.wireOp",EDGE,"E302"),sQuery(id+"F53.wireOp",EDGE,"E304")])]})});
            fillet(context, id + "F55", {"entities" : qUnion([Q0, Q1, Q2, Q3]), "radius" : 5 * mm, "tangentPropagation" : true, "allowEdgeOverflow" : false});
        }
    });
